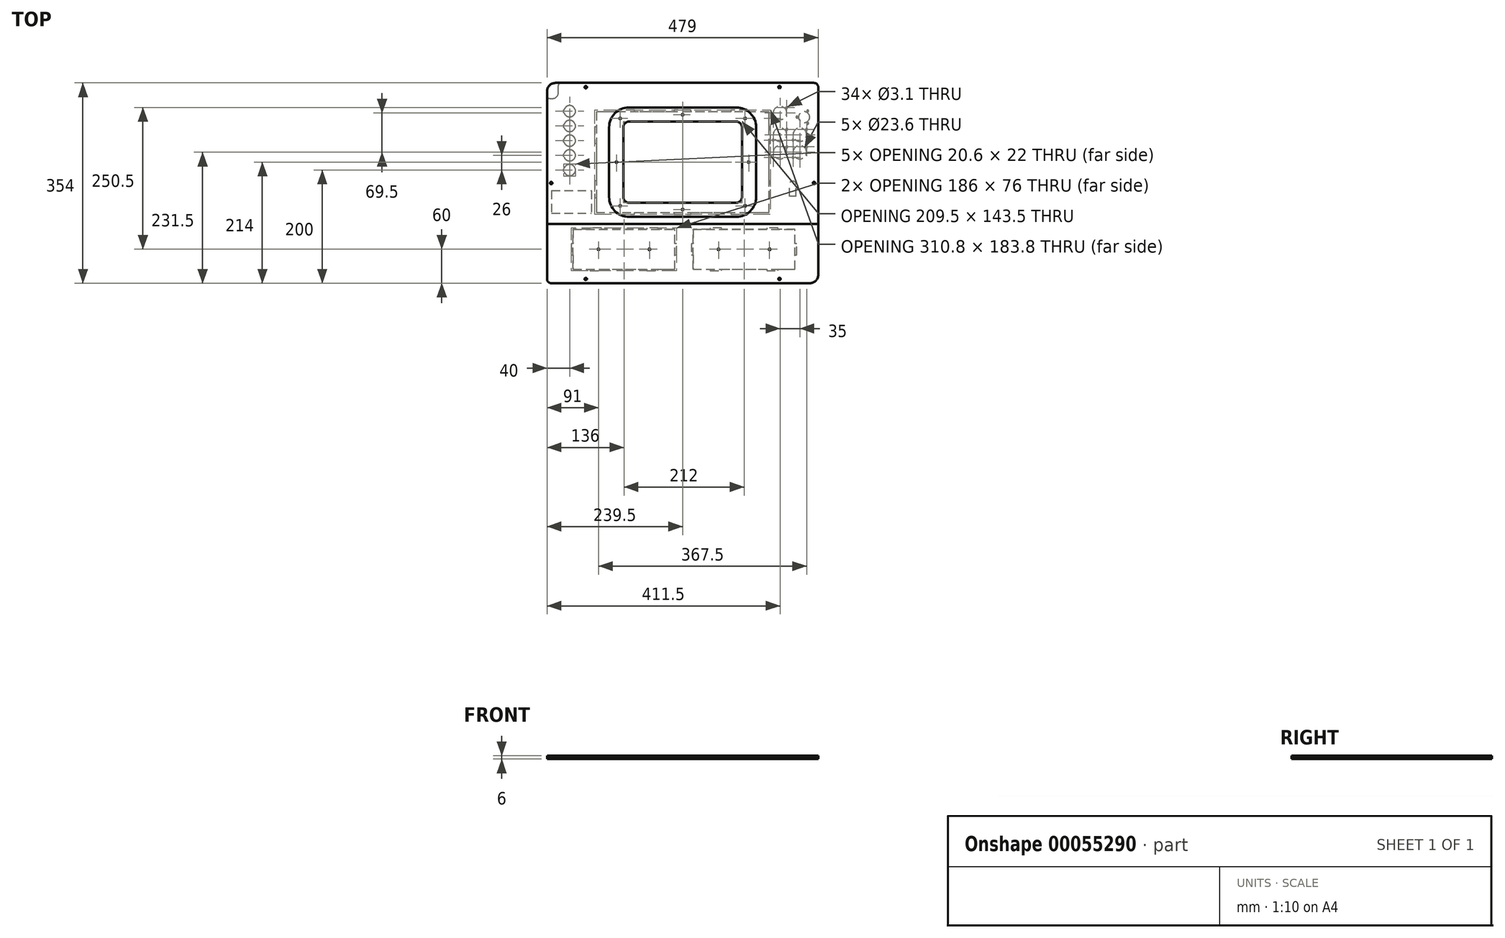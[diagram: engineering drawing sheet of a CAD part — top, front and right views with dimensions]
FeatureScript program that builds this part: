
annotation { "Feature Type Name" : "Feature", "Feature Type Description" : "" }
export const myFeature = defineFeature(function(context is Context, id is Id, definition is map)
    precondition{}
    {
        {
            assignVariable(context, id + "F0", {"name" : "PanelThickness", "anyValue" : 3});
        }
        {
            var Q0;
            Q0=qCreatedBy(makeId("Top.planeOp"),FACE);
            var sketch = newSketch(context, id + "F1", { "sketchPlane" : qUnion([Q0])});
            skPoint(sketch, "E0", {"position": v(168.5, 155) * mm});
            skPoint(sketch, "E1.visualSharp", {"position": v(237, -191.5) * mm});
            skPoint(sketch, "E2.visualSharp", {"position": v(-242, -191.5) * mm});
            skPoint(sketch, "E3.MirrorP", {"position": v(205.63, -175.57) * mm});
            skLineSegment(sketch, "E4.rect.right", {"start": v(237, 155) * mm, "end": v(237, -176.5) * mm});
            skPoint(sketch, "E5", {"position": v(229.5, -14.5) * mm});
            skPoint(sketch, "E6.visualSharp", {"position": v(-222, 135) * mm});
            skPoint(sketch, "E7.visualSharp", {"position": v(237, 162.5) * mm});
            skLineSegment(sketch, "E8", {"start": v(-249.24, -14.5) * mm, "end": v(312.3, -14.5) * mm, "construction": true});
            skPoint(sketch, "E9", {"position": v(-173.5, 155) * mm});
            skPoint(sketch, "E10.visualSharp", {"position": v(-242, 162.5) * mm});
            skLineSegment(sketch, "E11", {"start": v(0, 162.5) * mm, "end": v(0, -191.5) * mm, "construction": true});
            skLineSegment(sketch, "E12.0", {"start": v(-224.5, 155) * mm, "end": v(224.5, 155) * mm, "construction": true});
            skLineSegment(sketch, "E13.0", {"start": v(-242, -184) * mm, "end": v(224.5, -184) * mm, "construction": true});
            skLineSegment(sketch, "E14.0", {"start": v(-234.5, 162.5) * mm, "end": v(-234.5, -191.5) * mm, "construction": true});
            skLineSegment(sketch, "E4.rect.top", {"start": v(-234.5, -191.5) * mm, "end": v(222, -191.5) * mm});
            skLineSegment(sketch, "E4.rect.left", {"start": v(-242, 130) * mm, "end": v(-242, -184) * mm});
            skPoint(sketch, "E15", {"position": v(-234.5, -14.5) * mm});
            skLineSegment(sketch, "E4.rect.bottom", {"start": v(-217, 162.5) * mm, "end": v(229.5, 162.5) * mm});
            skLineSegment(sketch, "E16", {"start": v(168.5, -197.31) * mm, "end": v(168.5, 217.61) * mm, "construction": true});
            skLineSegment(sketch, "E17", {"start": v(-173.5, 192.32) * mm, "end": v(-173.5, -229.31) * mm, "construction": true});
            skLineSegment(sketch, "E18.0", {"start": v(229.5, 162.5) * mm, "end": v(229.5, -191.5) * mm, "construction": true});
            skLineSegment(sketch, "E19.left", {"start": v(-242, 146.2) * mm, "end": v(-242, 155) * mm, "construction": true});
            skLineSegment(sketch, "E19.bottom", {"start": v(-237, 135) * mm, "end": v(-232, 135) * mm});
            skCircle(sketch, "E20", {"center": v(-173.5, -184) * mm, "radius": 2.1 * mm});
            skArc(sketch, "E7.filletArc", {"start": v(237, 155) * mm, "mid": v(234.8, 160.3) * mm, "end": v(229.5, 162.5) * mm});
            skArc(sketch, "E6.filletArc", {"start": v(-232, 135) * mm, "mid": v(-224.93, 137.93) * mm, "end": v(-222, 145) * mm});
            skCircle(sketch, "E21", {"center": v(168.5, 155) * mm, "radius": 2.1 * mm});
            skCircle(sketch, "E22", {"center": v(229.5, -14.5) * mm, "radius": 2.1 * mm});
            skCircle(sketch, "E23", {"center": v(168.5, -184) * mm, "radius": 2.1 * mm});
            skCircle(sketch, "E24", {"center": v(-234.5, -14.5) * mm, "radius": 2.1 * mm});
            skCircle(sketch, "E25", {"center": v(-173.5, 155) * mm, "radius": 2.1 * mm});
            skArc(sketch, "E2.filletArc", {"start": v(-242, -184) * mm, "mid": v(-239.8, -189.3) * mm, "end": v(-234.5, -191.5) * mm});
            skArc(sketch, "E1.filletArc", {"start": v(222, -191.5) * mm, "mid": v(232.6, -187.1) * mm, "end": v(237, -176.5) * mm});
            skLineSegment(sketch, "E19.right", {"start": v(-222, 145) * mm, "end": v(-222, 157.5) * mm});
            skArc(sketch, "E26.filletArc", {"start": v(-237, 135) * mm, "mid": v(-240.54, 133.54) * mm, "end": v(-242, 130) * mm});
            skArc(sketch, "E27.filletArc", {"start": v(-217, 162.5) * mm, "mid": v(-220.54, 161.04) * mm, "end": v(-222, 157.5) * mm});
            skPoint(sketch, "E28", {"position": v(0, -14.5) * mm});
            skLineSegment(sketch, "E29", {"start": v(-242, 140) * mm, "end": v(-242, 130) * mm, "construction": true});
            skLineSegment(sketch, "E30", {"start": v(-234.5, 162.5) * mm, "end": v(-217, 162.5) * mm, "construction": true});
            skLineSegment(sketch, "E31", {"start": v(-242, 130) * mm, "end": v(-242, 147.5) * mm});
            skLineSegment(sketch, "E32", {"start": v(-227, 162.5) * mm, "end": v(-217, 162.5) * mm});
            skArc(sketch, "E33.filletArc", {"start": v(-227, 162.5) * mm, "mid": v(-237.6, 158.1) * mm, "end": v(-242, 147.5) * mm});
            skSolve(sketch);
        }
        {
            var Q0;
            Q0=qCreatedBy(makeId("Top.planeOp"),FACE);
            var sketch = newSketch(context, id + "F2", { "sketchPlane" : qUnion([Q0])});
            skLineSegment(sketch, "E34.bottom", {"start": v(-234, -28) * mm, "end": v(-163.5, -28) * mm});
            skLineSegment(sketch, "E34.top", {"start": v(-234, -67.5) * mm, "end": v(-163.5, -67.5) * mm});
            skLineSegment(sketch, "E34.right", {"start": v(-163.5, -28) * mm, "end": v(-163.5, -67.5) * mm});
            skLineSegment(sketch, "E34.left", {"start": v(-234, -28) * mm, "end": v(-234, -67.5) * mm});
            skLineSegment(sketch, "E35.0", {"start": v(-242, 130) * mm, "end": v(-242, -184) * mm});
            skLineSegment(sketch, "E36.0", {"start": v(-217, 162.5) * mm, "end": v(229.5, 162.5) * mm});
            skLineSegment(sketch, "E37.1", {"start": v(-238.1, -25.9) * mm, "end": v(-159.4, -25.9) * mm, "construction": true});
            skLineSegment(sketch, "E38.0", {"start": v(-159.4, -25.9) * mm, "end": v(-159.4, -69.6) * mm, "construction": true});
            skLineSegment(sketch, "E39.0", {"start": v(-238.1, -25.9) * mm, "end": v(-238.1, -69.6) * mm, "construction": true});
            skLineSegment(sketch, "E40.0", {"start": v(-238.1, -69.6) * mm, "end": v(-159.4, -69.6) * mm, "construction": true});
            skSolve(sketch);
        }
        {
            var Q0;
            Q0=qCreatedBy(makeId("Top.planeOp"),FACE);
            var sketch = newSketch(context, id + "F3", { "sketchPlane" : qUnion([Q0])});
            skLineSegment(sketch, "E41", {"start": v(0, 58.76) * mm, "end": v(0, -203.67) * mm, "construction": true});
            skLineSegment(sketch, "E42", {"start": v(-178.62, -14.5) * mm, "end": v(136.76, -14.5) * mm, "construction": true});
            skLineSegment(sketch, "E43", {"start": v(-16, -141.5) * mm, "end": v(-16, -166.5) * mm});
            skLineSegment(sketch, "E44", {"start": v(-166, -96.5) * mm, "end": v(-196, -96.5) * mm});
            skLineSegment(sketch, "E45.0", {"start": v(-13, -93.5) * mm, "end": v(-13, -169.5) * mm, "construction": true});
            skLineSegment(sketch, "E46", {"start": v(-166, -166.5) * mm, "end": v(-196, -166.5) * mm});
            skLineSegment(sketch, "E47.MirrorCS", {"start": v(-66, -93.5) * mm, "end": v(-46, -93.5) * mm});
            skLineSegment(sketch, "E48.rect.bottom", {"start": v(-16, -96.5) * mm, "end": v(-46, -96.5) * mm});
            skLineSegment(sketch, "E48.rect.top", {"start": v(-16, -166.5) * mm, "end": v(-46, -166.5) * mm});
            skLineSegment(sketch, "E48.rect.left", {"start": v(-16, -96.5) * mm, "end": v(-16, -121.5) * mm});
            skLineSegment(sketch, "E48.rect.right", {"start": v(-196, -96.5) * mm, "end": v(-196, -121.5) * mm});
            skPoint(sketch, "E49", {"position": v(-199, -131.5) * mm});
            skLineSegment(sketch, "E50.top", {"start": v(-66, -169.5) * mm, "end": v(-46, -169.5) * mm});
            skLineSegment(sketch, "E51.MirrorCS", {"start": v(-146, -169.5) * mm, "end": v(-166, -169.5) * mm});
            skLineSegment(sketch, "E52", {"start": v(-66, -96.5) * mm, "end": v(-146, -96.5) * mm});
            skLineSegment(sketch, "E53.0", {"start": v(-13, -169.5) * mm, "end": v(-199, -169.5) * mm, "construction": true});
            skLineSegment(sketch, "E54.0", {"start": v(-199, -93.5) * mm, "end": v(-199, -169.5) * mm, "construction": true});
            skLineSegment(sketch, "E55.0", {"start": v(-13, -93.5) * mm, "end": v(-199, -93.5) * mm, "construction": true});
            skLineSegment(sketch, "E56", {"start": v(-196, -141.5) * mm, "end": v(-196, -166.5) * mm});
            skLineSegment(sketch, "E57.MirrorCS", {"start": v(-13, -141.5) * mm, "end": v(-13, -121.5) * mm});
            skLineSegment(sketch, "E58", {"start": v(-66, -166.5) * mm, "end": v(-146, -166.5) * mm});
            skLineSegment(sketch, "E59.right", {"start": v(-199, -141.5) * mm, "end": v(-199, -121.5) * mm});
            skLineSegment(sketch, "E60.MirrorCS", {"start": v(-16, -121.5) * mm, "end": v(-13, -121.5) * mm});
            skLineSegment(sketch, "E61.MirrorCS", {"start": v(-16, -141.5) * mm, "end": v(-13, -141.5) * mm});
            skLineSegment(sketch, "E59.top", {"start": v(-196, -121.5) * mm, "end": v(-199, -121.5) * mm});
            skLineSegment(sketch, "E62.MirrorCS", {"start": v(-66, -96.5) * mm, "end": v(-66, -93.5) * mm});
            skLineSegment(sketch, "E63.MirrorCS", {"start": v(-46, -96.5) * mm, "end": v(-46, -93.5) * mm});
            skLineSegment(sketch, "E50.left", {"start": v(-66, -166.5) * mm, "end": v(-66, -169.5) * mm});
            skLineSegment(sketch, "E50.right", {"start": v(-46, -166.5) * mm, "end": v(-46, -169.5) * mm});
            skLineSegment(sketch, "E64.MirrorCS", {"start": v(-146, -166.5) * mm, "end": v(-146, -169.5) * mm});
            skLineSegment(sketch, "E65.MirrorCS", {"start": v(-166, -166.5) * mm, "end": v(-166, -169.5) * mm});
            skLineSegment(sketch, "E59.bottom", {"start": v(-196, -141.5) * mm, "end": v(-199, -141.5) * mm});
            skLineSegment(sketch, "E66.MirrorCS", {"start": v(16, -121.5) * mm, "end": v(13, -121.5) * mm});
            skLineSegment(sketch, "E67.MirrorCS", {"start": v(16, -141.5) * mm, "end": v(13, -141.5) * mm});
            skPoint(sketch, "E68.MirrorP", {"position": v(199, -131.5) * mm});
            skLineSegment(sketch, "E69.MirrorCS", {"start": v(146, -96.5) * mm, "end": v(146, -93.5) * mm});
            skLineSegment(sketch, "E70.MirrorCS", {"start": v(199, -93.5) * mm, "end": v(199, -169.5) * mm, "construction": true});
            skLineSegment(sketch, "E71.MirrorCS", {"start": v(166, -96.5) * mm, "end": v(166, -93.5) * mm});
            skLineSegment(sketch, "E72.MirrorCS", {"start": v(13, -93.5) * mm, "end": v(199, -93.5) * mm, "construction": true});
            skLineSegment(sketch, "E73.MirrorCS", {"start": v(196, -141.5) * mm, "end": v(199, -141.5) * mm});
            skLineSegment(sketch, "E74.MirrorCS", {"start": v(16, -141.5) * mm, "end": v(16, -166.5) * mm});
            skLineSegment(sketch, "E75.MirrorCS", {"start": v(196, -141.5) * mm, "end": v(196, -166.5) * mm});
            skLineSegment(sketch, "E76.MirrorCS", {"start": v(13, -141.5) * mm, "end": v(13, -121.5) * mm});
            skLineSegment(sketch, "E77.MirrorCS", {"start": v(166, -96.5) * mm, "end": v(196, -96.5) * mm});
            skLineSegment(sketch, "E78.MirrorCS", {"start": v(66, -166.5) * mm, "end": v(146, -166.5) * mm});
            skLineSegment(sketch, "E79.MirrorCS", {"start": v(13, -93.5) * mm, "end": v(13, -169.5) * mm, "construction": true});
            skLineSegment(sketch, "E80.MirrorCS", {"start": v(199, -141.5) * mm, "end": v(199, -121.5) * mm});
            skLineSegment(sketch, "E81.MirrorCS", {"start": v(166, -166.5) * mm, "end": v(196, -166.5) * mm});
            skLineSegment(sketch, "E82.MirrorCS", {"start": v(13, -169.5) * mm, "end": v(199, -169.5) * mm, "construction": true});
            skLineSegment(sketch, "E83.MirrorCS", {"start": v(66, -93.5) * mm, "end": v(46, -93.5) * mm});
            skLineSegment(sketch, "E84.MirrorCS", {"start": v(16, -96.5) * mm, "end": v(46, -96.5) * mm});
            skLineSegment(sketch, "E85.MirrorCS", {"start": v(66, -96.5) * mm, "end": v(66, -93.5) * mm});
            skLineSegment(sketch, "E86.MirrorCS", {"start": v(16, -96.5) * mm, "end": v(16, -121.5) * mm});
            skLineSegment(sketch, "E87.MirrorCS", {"start": v(46, -96.5) * mm, "end": v(46, -93.5) * mm});
            skLineSegment(sketch, "E88.MirrorCS", {"start": v(196, -96.5) * mm, "end": v(196, -121.5) * mm});
            skLineSegment(sketch, "E89.MirrorCS", {"start": v(66, -166.5) * mm, "end": v(66, -169.5) * mm});
            skLineSegment(sketch, "E90.MirrorCS", {"start": v(66, -169.5) * mm, "end": v(46, -169.5) * mm});
            skLineSegment(sketch, "E91.MirrorCS", {"start": v(46, -166.5) * mm, "end": v(46, -169.5) * mm});
            skLineSegment(sketch, "E92.MirrorCS", {"start": v(146, -169.5) * mm, "end": v(166, -169.5) * mm});
            skLineSegment(sketch, "E93.MirrorCS", {"start": v(146, -166.5) * mm, "end": v(146, -169.5) * mm});
            skLineSegment(sketch, "E94.MirrorCS", {"start": v(146, -93.5) * mm, "end": v(166, -93.5) * mm});
            skLineSegment(sketch, "E95.MirrorCS", {"start": v(16, -166.5) * mm, "end": v(46, -166.5) * mm});
            skLineSegment(sketch, "E96.MirrorCS", {"start": v(196, -121.5) * mm, "end": v(199, -121.5) * mm});
            skLineSegment(sketch, "E97.MirrorCS", {"start": v(66, -96.5) * mm, "end": v(146, -96.5) * mm});
            skLineSegment(sketch, "E98.MirrorCS", {"start": v(166, -166.5) * mm, "end": v(166, -169.5) * mm});
            skPoint(sketch, "E99", {"position": v(0, -14.5) * mm});
            skLineSegment(sketch, "E100", {"start": v(-199, -131.5) * mm, "end": v(-13, -131.5) * mm, "construction": true});
            skLineSegment(sketch, "E101.MirrorCS", {"start": v(-166, -96.5) * mm, "end": v(-166, -93.5) * mm});
            skLineSegment(sketch, "E102.MirrorCS", {"start": v(-146, -93.5) * mm, "end": v(-166, -93.5) * mm});
            skLineSegment(sketch, "E103.MirrorCS", {"start": v(-146, -96.5) * mm, "end": v(-146, -93.5) * mm});
            skPoint(sketch, "E104", {"position": v(-106, -131.5) * mm});
            skLineSegment(sketch, "E105", {"start": v(-106, -96.5) * mm, "end": v(-106, -166.5) * mm, "construction": true});
            skLineSegment(sketch, "E106.0", {"start": v(-249.24, -14.5) * mm, "end": v(312.3, -14.5) * mm, "construction": true});
            skSolve(sketch);
        }
        {
            var Q0;
            Q0=qCreatedBy(makeId("Top.planeOp"),FACE);
            var sketch = newSketch(context, id + "F4", { "sketchPlane" : qUnion([Q0])});
            skLineSegment(sketch, "E107.0", {"start": v(-242, 130) * mm, "end": v(-242, -184) * mm});
            skLineSegment(sketch, "E107.1", {"start": v(-217, 162.5) * mm, "end": v(229.5, 162.5) * mm});
            skPoint(sketch, "E108", {"position": v(-202, 115.3) * mm});
            skPoint(sketch, "E109", {"position": v(-200.95, 112.5) * mm});
            skPoint(sketch, "E110", {"position": v(-202, 109.7) * mm});
            skArc(sketch, "E111", {"start": v(-200.95, 102.56) * mm, "mid": v(-195.59, 104.83) * mm, "end": v(-192.4, 109.7) * mm});
            skArc(sketch, "E112", {"start": v(-211.6, 109.7) * mm, "mid": v(-208.41, 104.83) * mm, "end": v(-203.05, 102.56) * mm});
            skArc(sketch, "E113", {"start": v(-192.4, 115.3) * mm, "mid": v(-195.59, 120.17) * mm, "end": v(-200.95, 122.44) * mm});
            skPoint(sketch, "E114", {"position": v(-203.05, 112.5) * mm});
            skArc(sketch, "E115", {"start": v(-203.05, 122.44) * mm, "mid": v(-208.41, 120.17) * mm, "end": v(-211.6, 115.3) * mm});
            skCircle(sketch, "E116", {"center": v(-202, 112.5) * mm, "radius": 11.5 * mm, "construction": true});
            skLineSegment(sketch, "E117", {"start": v(-192.4, 115.3) * mm, "end": v(-211.6, 115.3) * mm, "construction": true});
            skLineSegment(sketch, "E118", {"start": v(-200.95, 122.44) * mm, "end": v(-200.95, 102.56) * mm, "construction": true});
            skLineSegment(sketch, "E119", {"start": v(-192.4, 109.7) * mm, "end": v(-211.6, 109.7) * mm, "construction": true});
            skLineSegment(sketch, "E120", {"start": v(-203.05, 122.44) * mm, "end": v(-203.05, 102.56) * mm, "construction": true});
            skLineSegment(sketch, "E121", {"start": v(-191.7, 112.5) * mm, "end": v(-212.3, 112.5) * mm, "construction": true});
            skLineSegment(sketch, "E122", {"start": v(-202, 123.5) * mm, "end": v(-202, 101.5) * mm, "construction": true});
            skLineSegment(sketch, "E123", {"start": v(-192.4, 115.3) * mm, "end": v(-191.7, 115.3) * mm});
            skLineSegment(sketch, "E124", {"start": v(-211.6, 115.3) * mm, "end": v(-212.3, 115.3) * mm});
            skLineSegment(sketch, "E125", {"start": v(-203.05, 102.56) * mm, "end": v(-203.05, 101.5) * mm});
            skLineSegment(sketch, "E126", {"start": v(-200.95, 101.5) * mm, "end": v(-203.05, 101.5) * mm});
            skLineSegment(sketch, "E127.rect.right", {"start": v(-212.3, 109.7) * mm, "end": v(-212.3, 115.3) * mm});
            skLineSegment(sketch, "E127.rect.left", {"start": v(-191.7, 109.7) * mm, "end": v(-191.7, 115.3) * mm});
            skLineSegment(sketch, "E127.rect.bottom", {"start": v(-191.7, 109.7) * mm, "end": v(-192.4, 109.7) * mm});
            skLineSegment(sketch, "E128", {"start": v(-211.6, 109.7) * mm, "end": v(-212.3, 109.7) * mm});
            skLineSegment(sketch, "E129", {"start": v(-200.95, 102.56) * mm, "end": v(-200.95, 101.5) * mm});
            skLineSegment(sketch, "E130.MirrorCS", {"start": v(-203.05, 122.44) * mm, "end": v(-203.05, 123.5) * mm});
            skLineSegment(sketch, "E131.MirrorCS", {"start": v(-200.95, 122.44) * mm, "end": v(-200.95, 123.5) * mm});
            skLineSegment(sketch, "E132.MirrorCS", {"start": v(-200.95, 123.5) * mm, "end": v(-203.05, 123.5) * mm});
            skCircle(sketch, "E133.0.1.0", {"center": v(-202, 86.5) * mm, "radius": 11.5 * mm, "construction": true});
            skPoint(sketch, "E133.0.1.1", {"position": v(-203.05, 86.5) * mm});
            skLineSegment(sketch, "E133.0.1.2", {"start": v(-202, 97.5) * mm, "end": v(-202, 75.5) * mm, "construction": true});
            skArc(sketch, "E133.0.1.3", {"start": v(-200.95, 76.56) * mm, "mid": v(-195.59, 78.83) * mm, "end": v(-192.4, 83.7) * mm});
            skLineSegment(sketch, "E133.0.1.4", {"start": v(-212.3, 83.7) * mm, "end": v(-212.3, 89.3) * mm});
            skLineSegment(sketch, "E133.0.1.5", {"start": v(-200.95, 96.44) * mm, "end": v(-200.95, 76.56) * mm, "construction": true});
            skArc(sketch, "E133.0.1.6", {"start": v(-203.05, 96.44) * mm, "mid": v(-208.41, 94.17) * mm, "end": v(-211.6, 89.3) * mm});
            skLineSegment(sketch, "E133.0.1.7", {"start": v(-191.7, 86.5) * mm, "end": v(-212.3, 86.5) * mm, "construction": true});
            skLineSegment(sketch, "E133.0.1.8", {"start": v(-203.05, 96.44) * mm, "end": v(-203.05, 76.56) * mm, "construction": true});
            skPoint(sketch, "E133.0.1.9", {"position": v(-202, 83.7) * mm});
            skPoint(sketch, "E133.0.1.10", {"position": v(-202, 86.5) * mm});
            skArc(sketch, "E133.0.1.11", {"start": v(-192.4, 89.3) * mm, "mid": v(-195.59, 94.17) * mm, "end": v(-200.95, 96.44) * mm});
            skPoint(sketch, "E133.0.1.12", {"position": v(-200.95, 86.5) * mm});
            skLineSegment(sketch, "E133.0.1.13", {"start": v(-192.4, 89.3) * mm, "end": v(-211.6, 89.3) * mm, "construction": true});
            skPoint(sketch, "E133.0.1.14", {"position": v(-202, 89.3) * mm});
            skLineSegment(sketch, "E133.0.1.15", {"start": v(-191.7, 83.7) * mm, "end": v(-191.7, 89.3) * mm});
            skLineSegment(sketch, "E133.0.1.16", {"start": v(-192.4, 83.7) * mm, "end": v(-211.6, 83.7) * mm, "construction": true});
            skArc(sketch, "E133.0.1.17", {"start": v(-211.6, 83.7) * mm, "mid": v(-208.41, 78.83) * mm, "end": v(-203.05, 76.56) * mm});
            skPoint(sketch, "E133.0.1.18", {"position": v(-202, 86.5) * mm});
            skLineSegment(sketch, "E133.0.1.19", {"start": v(-200.95, 75.5) * mm, "end": v(-203.05, 75.5) * mm});
            skLineSegment(sketch, "E133.0.1.20", {"start": v(-192.4, 89.3) * mm, "end": v(-191.7, 89.3) * mm});
            skLineSegment(sketch, "E133.0.1.21", {"start": v(-200.95, 97.5) * mm, "end": v(-203.05, 97.5) * mm});
            skLineSegment(sketch, "E133.0.1.22", {"start": v(-203.05, 96.44) * mm, "end": v(-203.05, 97.5) * mm});
            skLineSegment(sketch, "E133.0.1.23", {"start": v(-203.05, 76.56) * mm, "end": v(-203.05, 75.5) * mm});
            skLineSegment(sketch, "E133.0.1.24", {"start": v(-191.7, 83.7) * mm, "end": v(-192.4, 83.7) * mm});
            skLineSegment(sketch, "E133.0.1.25", {"start": v(-200.95, 76.56) * mm, "end": v(-200.95, 75.5) * mm});
            skLineSegment(sketch, "E133.0.1.26", {"start": v(-211.6, 83.7) * mm, "end": v(-212.3, 83.7) * mm});
            skLineSegment(sketch, "E133.0.1.27", {"start": v(-200.95, 96.44) * mm, "end": v(-200.95, 97.5) * mm});
            skLineSegment(sketch, "E133.0.1.28", {"start": v(-211.6, 89.3) * mm, "end": v(-212.3, 89.3) * mm});
            skCircle(sketch, "E133.0.2.0", {"center": v(-202, 60.5) * mm, "radius": 11.5 * mm, "construction": true});
            skPoint(sketch, "E133.0.2.1", {"position": v(-203.05, 60.5) * mm});
            skLineSegment(sketch, "E133.0.2.2", {"start": v(-202, 71.5) * mm, "end": v(-202, 49.5) * mm, "construction": true});
            skArc(sketch, "E133.0.2.3", {"start": v(-200.95, 50.56) * mm, "mid": v(-195.59, 52.83) * mm, "end": v(-192.4, 57.7) * mm});
            skLineSegment(sketch, "E133.0.2.4", {"start": v(-212.3, 57.7) * mm, "end": v(-212.3, 63.3) * mm});
            skLineSegment(sketch, "E133.0.2.5", {"start": v(-200.95, 70.44) * mm, "end": v(-200.95, 50.56) * mm, "construction": true});
            skArc(sketch, "E133.0.2.6", {"start": v(-203.05, 70.44) * mm, "mid": v(-208.41, 68.17) * mm, "end": v(-211.6, 63.3) * mm});
            skLineSegment(sketch, "E133.0.2.7", {"start": v(-191.7, 60.5) * mm, "end": v(-212.3, 60.5) * mm, "construction": true});
            skLineSegment(sketch, "E133.0.2.8", {"start": v(-203.05, 70.44) * mm, "end": v(-203.05, 50.56) * mm, "construction": true});
            skPoint(sketch, "E133.0.2.9", {"position": v(-202, 57.7) * mm});
            skPoint(sketch, "E133.0.2.10", {"position": v(-202, 60.5) * mm});
            skArc(sketch, "E133.0.2.11", {"start": v(-192.4, 63.3) * mm, "mid": v(-195.59, 68.17) * mm, "end": v(-200.95, 70.44) * mm});
            skPoint(sketch, "E133.0.2.12", {"position": v(-200.95, 60.5) * mm});
            skLineSegment(sketch, "E133.0.2.13", {"start": v(-192.4, 63.3) * mm, "end": v(-211.6, 63.3) * mm, "construction": true});
            skPoint(sketch, "E133.0.2.14", {"position": v(-202, 63.3) * mm});
            skLineSegment(sketch, "E133.0.2.15", {"start": v(-191.7, 57.7) * mm, "end": v(-191.7, 63.3) * mm});
            skLineSegment(sketch, "E133.0.2.16", {"start": v(-192.4, 57.7) * mm, "end": v(-211.6, 57.7) * mm, "construction": true});
            skArc(sketch, "E133.0.2.17", {"start": v(-211.6, 57.7) * mm, "mid": v(-208.41, 52.83) * mm, "end": v(-203.05, 50.56) * mm});
            skPoint(sketch, "E133.0.2.18", {"position": v(-202, 60.5) * mm});
            skLineSegment(sketch, "E133.0.2.19", {"start": v(-200.95, 49.5) * mm, "end": v(-203.05, 49.5) * mm});
            skLineSegment(sketch, "E133.0.2.20", {"start": v(-192.4, 63.3) * mm, "end": v(-191.7, 63.3) * mm});
            skLineSegment(sketch, "E133.0.2.21", {"start": v(-200.95, 71.5) * mm, "end": v(-203.05, 71.5) * mm});
            skLineSegment(sketch, "E133.0.2.22", {"start": v(-203.05, 70.44) * mm, "end": v(-203.05, 71.5) * mm});
            skLineSegment(sketch, "E133.0.2.23", {"start": v(-203.05, 50.56) * mm, "end": v(-203.05, 49.5) * mm});
            skLineSegment(sketch, "E133.0.2.24", {"start": v(-191.7, 57.7) * mm, "end": v(-192.4, 57.7) * mm});
            skLineSegment(sketch, "E133.0.2.25", {"start": v(-200.95, 50.56) * mm, "end": v(-200.95, 49.5) * mm});
            skLineSegment(sketch, "E133.0.2.26", {"start": v(-211.6, 57.7) * mm, "end": v(-212.3, 57.7) * mm});
            skLineSegment(sketch, "E133.0.2.27", {"start": v(-200.95, 70.44) * mm, "end": v(-200.95, 71.5) * mm});
            skLineSegment(sketch, "E133.0.2.28", {"start": v(-211.6, 63.3) * mm, "end": v(-212.3, 63.3) * mm});
            skCircle(sketch, "E133.0.3.0", {"center": v(-202, 34.5) * mm, "radius": 11.5 * mm, "construction": true});
            skPoint(sketch, "E133.0.3.1", {"position": v(-203.05, 34.5) * mm});
            skLineSegment(sketch, "E133.0.3.2", {"start": v(-202, 45.5) * mm, "end": v(-202, 23.5) * mm, "construction": true});
            skArc(sketch, "E133.0.3.3", {"start": v(-200.95, 24.56) * mm, "mid": v(-195.59, 26.83) * mm, "end": v(-192.4, 31.7) * mm});
            skLineSegment(sketch, "E133.0.3.4", {"start": v(-212.3, 31.7) * mm, "end": v(-212.3, 37.3) * mm});
            skLineSegment(sketch, "E133.0.3.5", {"start": v(-200.95, 44.44) * mm, "end": v(-200.95, 24.56) * mm, "construction": true});
            skArc(sketch, "E133.0.3.6", {"start": v(-203.05, 44.44) * mm, "mid": v(-208.41, 42.17) * mm, "end": v(-211.6, 37.3) * mm});
            skLineSegment(sketch, "E133.0.3.7", {"start": v(-191.7, 34.5) * mm, "end": v(-212.3, 34.5) * mm, "construction": true});
            skLineSegment(sketch, "E133.0.3.8", {"start": v(-203.05, 44.44) * mm, "end": v(-203.05, 24.56) * mm, "construction": true});
            skPoint(sketch, "E133.0.3.9", {"position": v(-202, 31.7) * mm});
            skPoint(sketch, "E133.0.3.10", {"position": v(-202, 34.5) * mm});
            skArc(sketch, "E133.0.3.11", {"start": v(-192.4, 37.3) * mm, "mid": v(-195.59, 42.17) * mm, "end": v(-200.95, 44.44) * mm});
            skPoint(sketch, "E133.0.3.12", {"position": v(-200.95, 34.5) * mm});
            skLineSegment(sketch, "E133.0.3.13", {"start": v(-192.4, 37.3) * mm, "end": v(-211.6, 37.3) * mm, "construction": true});
            skPoint(sketch, "E133.0.3.14", {"position": v(-202, 37.3) * mm});
            skLineSegment(sketch, "E133.0.3.15", {"start": v(-191.7, 31.7) * mm, "end": v(-191.7, 37.3) * mm});
            skLineSegment(sketch, "E133.0.3.16", {"start": v(-192.4, 31.7) * mm, "end": v(-211.6, 31.7) * mm, "construction": true});
            skArc(sketch, "E133.0.3.17", {"start": v(-211.6, 31.7) * mm, "mid": v(-208.41, 26.83) * mm, "end": v(-203.05, 24.56) * mm});
            skPoint(sketch, "E133.0.3.18", {"position": v(-202, 34.5) * mm});
            skLineSegment(sketch, "E133.0.3.19", {"start": v(-200.95, 23.5) * mm, "end": v(-203.05, 23.5) * mm});
            skLineSegment(sketch, "E133.0.3.20", {"start": v(-192.4, 37.3) * mm, "end": v(-191.7, 37.3) * mm});
            skLineSegment(sketch, "E133.0.3.21", {"start": v(-200.95, 45.5) * mm, "end": v(-203.05, 45.5) * mm});
            skLineSegment(sketch, "E133.0.3.22", {"start": v(-203.05, 44.44) * mm, "end": v(-203.05, 45.5) * mm});
            skLineSegment(sketch, "E133.0.3.23", {"start": v(-203.05, 24.56) * mm, "end": v(-203.05, 23.5) * mm});
            skLineSegment(sketch, "E133.0.3.24", {"start": v(-191.7, 31.7) * mm, "end": v(-192.4, 31.7) * mm});
            skLineSegment(sketch, "E133.0.3.25", {"start": v(-200.95, 24.56) * mm, "end": v(-200.95, 23.5) * mm});
            skLineSegment(sketch, "E133.0.3.26", {"start": v(-211.6, 31.7) * mm, "end": v(-212.3, 31.7) * mm});
            skLineSegment(sketch, "E133.0.3.27", {"start": v(-200.95, 44.44) * mm, "end": v(-200.95, 45.5) * mm});
            skLineSegment(sketch, "E133.0.3.28", {"start": v(-211.6, 37.3) * mm, "end": v(-212.3, 37.3) * mm});
            skLineSegment(sketch, "E133.direction1", {"start": v(-202, 112.5) * mm, "end": v(-181.18, 112.5) * mm, "construction": true});
            skLineSegment(sketch, "E133.direction2", {"start": v(-202, 112.5) * mm, "end": v(-202, 86.5) * mm, "construction": true});
            skCircle(sketch, "E134.0.0.4", {"center": v(-202, 8.5) * mm, "radius": 11.5 * mm, "construction": true});
            skPoint(sketch, "E134.2.0.4", {"position": v(-203.05, 8.5) * mm});
            skLineSegment(sketch, "E134.3.0.4", {"start": v(-202, 19.5) * mm, "end": v(-202, -2.5) * mm, "construction": true});
            skArc(sketch, "E134.6.0.4", {"start": v(-200.95, -1.44) * mm, "mid": v(-195.59, 0.83) * mm, "end": v(-192.4, 5.7) * mm});
            skLineSegment(sketch, "E134.10.0.4", {"start": v(-212.3, 5.7) * mm, "end": v(-212.3, 11.3) * mm});
            skLineSegment(sketch, "E134.13.0.4", {"start": v(-200.95, 18.44) * mm, "end": v(-200.95, -1.44) * mm, "construction": true});
            skArc(sketch, "E134.16.0.4", {"start": v(-203.05, 18.44) * mm, "mid": v(-208.41, 16.17) * mm, "end": v(-211.6, 11.3) * mm});
            skLineSegment(sketch, "E134.20.0.4", {"start": v(-191.7, 8.5) * mm, "end": v(-212.3, 8.5) * mm, "construction": true});
            skLineSegment(sketch, "E134.23.0.4", {"start": v(-203.05, 18.44) * mm, "end": v(-203.05, -1.44) * mm, "construction": true});
            skPoint(sketch, "E134.26.0.4", {"position": v(-202, 5.7) * mm});
            skPoint(sketch, "E134.27.0.4", {"position": v(-202, 8.5) * mm});
            skArc(sketch, "E134.28.0.4", {"start": v(-192.4, 11.3) * mm, "mid": v(-195.59, 16.17) * mm, "end": v(-200.95, 18.44) * mm});
            skPoint(sketch, "E134.32.0.4", {"position": v(-200.95, 8.5) * mm});
            skLineSegment(sketch, "E134.33.0.4", {"start": v(-192.4, 11.3) * mm, "end": v(-211.6, 11.3) * mm, "construction": true});
            skPoint(sketch, "E134.36.0.4", {"position": v(-202, 11.3) * mm});
            skLineSegment(sketch, "E134.37.0.4", {"start": v(-191.7, 5.7) * mm, "end": v(-191.7, 11.3) * mm});
            skLineSegment(sketch, "E134.40.0.4", {"start": v(-192.4, 5.7) * mm, "end": v(-211.6, 5.7) * mm, "construction": true});
            skArc(sketch, "E134.43.0.4", {"start": v(-211.6, 5.7) * mm, "mid": v(-208.41, 0.83) * mm, "end": v(-203.05, -1.44) * mm});
            skPoint(sketch, "E134.47.0.4", {"position": v(-202, 8.5) * mm});
            skLineSegment(sketch, "E134.48.0.4", {"start": v(-200.95, -2.5) * mm, "end": v(-203.05, -2.5) * mm});
            skLineSegment(sketch, "E134.51.0.4", {"start": v(-192.4, 11.3) * mm, "end": v(-191.7, 11.3) * mm});
            skLineSegment(sketch, "E134.54.0.4", {"start": v(-200.95, 19.5) * mm, "end": v(-203.05, 19.5) * mm});
            skLineSegment(sketch, "E134.57.0.4", {"start": v(-203.05, 18.44) * mm, "end": v(-203.05, 19.5) * mm});
            skLineSegment(sketch, "E134.60.0.4", {"start": v(-203.05, -1.44) * mm, "end": v(-203.05, -2.5) * mm});
            skLineSegment(sketch, "E134.63.0.4", {"start": v(-191.7, 5.7) * mm, "end": v(-192.4, 5.7) * mm});
            skLineSegment(sketch, "E134.66.0.4", {"start": v(-200.95, -1.44) * mm, "end": v(-200.95, -2.5) * mm});
            skLineSegment(sketch, "E134.69.0.4", {"start": v(-211.6, 5.7) * mm, "end": v(-212.3, 5.7) * mm});
            skLineSegment(sketch, "E134.72.0.4", {"start": v(-200.95, 18.44) * mm, "end": v(-200.95, 19.5) * mm});
            skLineSegment(sketch, "E134.75.0.4", {"start": v(-211.6, 11.3) * mm, "end": v(-212.3, 11.3) * mm});
            skSolve(sketch);
        }
        {
            var Q0;
            Q0=qCreatedBy(makeId("Top.planeOp"),FACE);
            var sketch = newSketch(context, id + "F5", { "sketchPlane" : qUnion([Q0])});
            skLineSegment(sketch, "E135", {"start": v(204.5, 59.2) * mm, "end": v(204.5, 132.46) * mm, "construction": true});
            skLineSegment(sketch, "E136.left", {"start": v(204.5, 71) * mm, "end": v(204.5, 84) * mm, "construction": true});
            skLineSegment(sketch, "E137.0", {"start": v(237, 155) * mm, "end": v(237, -176.5) * mm});
            skLineSegment(sketch, "E137.1", {"start": v(-217, 162.5) * mm, "end": v(229.5, 162.5) * mm});
            skCircle(sketch, "E138", {"center": v(212, 102) * mm, "radius": 12.5 * mm, "construction": true});
            skCircle(sketch, "E139", {"center": v(212, 102) * mm, "radius": 16 * mm, "construction": true});
            skCircle(sketch, "E140", {"center": v(199.5, 102) * mm, "radius": 1.75 * mm});
            skCircle(sketch, "E141.1.0", {"center": v(218.25, 91.17) * mm, "radius": 1.75 * mm});
            skCircle(sketch, "E141.2.0", {"center": v(218.25, 112.83) * mm, "radius": 1.75 * mm});
            skCircle(sketch, "E142", {"center": v(212, 102) * mm, "radius": 9.75 * mm});
            skPoint(sketch, "E143", {"position": v(177, 109.5) * mm});
            skLineSegment(sketch, "E144.MirrorCS", {"start": v(154, 109.5) * mm, "end": v(154, 96.5) * mm, "construction": true});
            skLineSegment(sketch, "E145.MirrorCS", {"start": v(169.5, 96.5) * mm, "end": v(154, 96.5) * mm, "construction": true});
            skLineSegment(sketch, "E146.MirrorCS", {"start": v(169.5, 96.5) * mm, "end": v(185, 96.5) * mm, "construction": true});
            skLineSegment(sketch, "E147.MirrorCS", {"start": v(185, 109.5) * mm, "end": v(185, 96.5) * mm, "construction": true});
            skLineSegment(sketch, "E148.left", {"start": v(169.5, 109.5) * mm, "end": v(169.5, 122.5) * mm, "construction": true});
            skLineSegment(sketch, "E148.top", {"start": v(169.5, 122.5) * mm, "end": v(154, 122.5) * mm, "construction": true});
            skLineSegment(sketch, "E148.bottom", {"start": v(169.5, 109.5) * mm, "end": v(161.52, 109.5) * mm, "construction": true});
            skLineSegment(sketch, "E149", {"start": v(169.5, 97.7) * mm, "end": v(169.5, 109.5) * mm, "construction": true});
            skCircle(sketch, "E150.MirrorC", {"center": v(169.5, 109.5) * mm, "radius": 11.8 * mm});
            skLineSegment(sketch, "E151", {"start": v(163.94, 109.5) * mm, "end": v(185, 109.5) * mm, "construction": true});
            skLineSegment(sketch, "E152.MirrorCS", {"start": v(185, 109.5) * mm, "end": v(185, 122.5) * mm, "construction": true});
            skLineSegment(sketch, "E148.right", {"start": v(154, 109.5) * mm, "end": v(154, 122.5) * mm, "construction": true});
            skLineSegment(sketch, "E153.MirrorCS", {"start": v(157.5, 95.86) * mm, "end": v(157.5, 88.51) * mm, "construction": true});
            skLineSegment(sketch, "E154.MirrorCS", {"start": v(192.3, 119) * mm, "end": v(186.5, 119) * mm, "construction": true});
            skLineSegment(sketch, "E155.MirrorCS", {"start": v(181.5, 114.86) * mm, "end": v(181.5, 108.38) * mm, "construction": true});
            skLineSegment(sketch, "E156.MirrorCS", {"start": v(169.5, 122.5) * mm, "end": v(185, 122.5) * mm, "construction": true});
            skCircle(sketch, "E157.MirrorC", {"center": v(181.5, 119) * mm, "radius": 1.55 * mm});
            skCircle(sketch, "E158.MirrorC", {"center": v(157.5, 100) * mm, "radius": 1.55 * mm});
            skLineSegment(sketch, "E159.MirrorCS", {"start": v(166.3, 100) * mm, "end": v(162.5, 100) * mm, "construction": true});
            skLineSegment(sketch, "E160.0.1.0", {"start": v(169.5, 66.7) * mm, "end": v(169.5, 78.5) * mm, "construction": true});
            skLineSegment(sketch, "E160.0.1.1", {"start": v(156.44, 71) * mm, "end": v(182.56, 71) * mm, "construction": true});
            skLineSegment(sketch, "E160.0.1.2", {"start": v(169.5, 91.5) * mm, "end": v(154, 91.5) * mm, "construction": true});
            skLineSegment(sketch, "E160.0.1.3", {"start": v(169.5, 78.5) * mm, "end": v(169.5, 91.5) * mm, "construction": true});
            skLineSegment(sketch, "E160.0.1.4", {"start": v(185, 71) * mm, "end": v(185, 58) * mm, "construction": true});
            skLineSegment(sketch, "E160.0.1.5", {"start": v(154, 78.5) * mm, "end": v(154, 91.5) * mm, "construction": true});
            skLineSegment(sketch, "E160.0.1.6", {"start": v(181.5, 83.86) * mm, "end": v(181.5, 77.38) * mm, "construction": true});
            skLineSegment(sketch, "E160.0.1.7", {"start": v(169.5, 84) * mm, "end": v(185, 84) * mm, "construction": true});
            skCircle(sketch, "E160.0.1.8", {"center": v(157.5, 61.5) * mm, "radius": 1.55 * mm});
            skLineSegment(sketch, "E160.0.1.9", {"start": v(184.8, 80.5) * mm, "end": v(179, 80.5) * mm, "construction": true});
            skCircle(sketch, "E160.0.1.10", {"center": v(169.5, 71) * mm, "radius": 11.8 * mm});
            skLineSegment(sketch, "E160.0.1.11", {"start": v(185, 71) * mm, "end": v(185, 84) * mm, "construction": true});
            skLineSegment(sketch, "E160.0.1.12", {"start": v(157.5, 64.86) * mm, "end": v(157.5, 57.51) * mm, "construction": true});
            skCircle(sketch, "E160.0.1.13", {"center": v(181.5, 80.5) * mm, "radius": 1.55 * mm});
            skLineSegment(sketch, "E160.0.1.14", {"start": v(169.5, 78.5) * mm, "end": v(154.02, 78.5) * mm, "construction": true});
            skLineSegment(sketch, "E160.0.1.15", {"start": v(169.5, 58) * mm, "end": v(185, 58) * mm, "construction": true});
            skLineSegment(sketch, "E160.0.1.16", {"start": v(169.5, 58) * mm, "end": v(154, 58) * mm, "construction": true});
            skLineSegment(sketch, "E160.0.1.17", {"start": v(154, 71) * mm, "end": v(154, 58) * mm, "construction": true});
            skPoint(sketch, "E160.0.1.18", {"position": v(169.5, 71) * mm});
            skLineSegment(sketch, "E160.0.1.19", {"start": v(158.8, 61.5) * mm, "end": v(155, 61.5) * mm, "construction": true});
            skCircle(sketch, "E160.0.1.20", {"center": v(169.5, 78.5) * mm, "radius": 11.8 * mm});
            skLineSegment(sketch, "E160.0.2.0", {"start": v(169.5, 28.2) * mm, "end": v(169.5, 40) * mm, "construction": true});
            skLineSegment(sketch, "E160.0.2.1", {"start": v(156.44, 40) * mm, "end": v(182.56, 40) * mm, "construction": true});
            skLineSegment(sketch, "E160.0.2.2", {"start": v(169.5, 53) * mm, "end": v(154, 53) * mm, "construction": true});
            skLineSegment(sketch, "E160.0.2.3", {"start": v(169.5, 40) * mm, "end": v(169.5, 53) * mm, "construction": true});
            skLineSegment(sketch, "E160.0.2.4", {"start": v(185, 40) * mm, "end": v(185, 27) * mm, "construction": true});
            skLineSegment(sketch, "E160.0.2.5", {"start": v(154, 40) * mm, "end": v(154, 53) * mm, "construction": true});
            skLineSegment(sketch, "E160.0.2.6", {"start": v(181.5, 52.86) * mm, "end": v(181.5, 46.38) * mm, "construction": true});
            skLineSegment(sketch, "E160.0.2.7", {"start": v(169.5, 53) * mm, "end": v(185, 53) * mm, "construction": true});
            skCircle(sketch, "E160.0.2.8", {"center": v(157.5, 30.5) * mm, "radius": 1.55 * mm});
            skLineSegment(sketch, "E160.0.2.9", {"start": v(184.8, 49.5) * mm, "end": v(179, 49.5) * mm, "construction": true});
            skCircle(sketch, "E160.0.2.10", {"center": v(169.5, 40) * mm, "radius": 11.8 * mm});
            skLineSegment(sketch, "E160.0.2.11", {"start": v(185, 40) * mm, "end": v(185, 53) * mm, "construction": true});
            skLineSegment(sketch, "E160.0.2.12", {"start": v(157.5, 33.86) * mm, "end": v(157.5, 26.51) * mm, "construction": true});
            skCircle(sketch, "E160.0.2.13", {"center": v(181.5, 49.5) * mm, "radius": 1.55 * mm});
            skLineSegment(sketch, "E160.0.2.14", {"start": v(169.5, 40) * mm, "end": v(154.02, 40) * mm, "construction": true});
            skLineSegment(sketch, "E160.0.2.15", {"start": v(169.5, 27) * mm, "end": v(185, 27) * mm, "construction": true});
            skLineSegment(sketch, "E160.0.2.16", {"start": v(169.5, 27) * mm, "end": v(154, 27) * mm, "construction": true});
            skLineSegment(sketch, "E160.0.2.17", {"start": v(154, 40) * mm, "end": v(154, 27) * mm, "construction": true});
            skPoint(sketch, "E160.0.2.18", {"position": v(169.5, 40) * mm});
            skLineSegment(sketch, "E160.0.2.19", {"start": v(158.8, 30.5) * mm, "end": v(155, 30.5) * mm, "construction": true});
            skCircle(sketch, "E160.0.2.20", {"center": v(169.5, 40) * mm, "radius": 11.8 * mm});
            skLineSegment(sketch, "E160.1.0.0", {"start": v(212, 89.5) * mm, "end": v(212, 102) * mm, "construction": true});
            skLineSegment(sketch, "E160.1.0.1", {"start": v(198.94, 102) * mm, "end": v(225.06, 102) * mm, "construction": true});
            skLineSegment(sketch, "E160.1.0.3", {"start": v(212, 102) * mm, "end": v(212, 114.5) * mm, "construction": true});
            skLineSegment(sketch, "E160.1.1.0", {"start": v(204.5, 59.2) * mm, "end": v(204.5, 71) * mm, "construction": true});
            skLineSegment(sketch, "E160.1.1.1", {"start": v(191.44, 71) * mm, "end": v(217.56, 71) * mm, "construction": true});
            skLineSegment(sketch, "E160.1.1.2", {"start": v(204.5, 84) * mm, "end": v(189, 84) * mm, "construction": true});
            skLineSegment(sketch, "E160.1.1.4", {"start": v(220, 71) * mm, "end": v(220, 58) * mm, "construction": true});
            skLineSegment(sketch, "E160.1.1.5", {"start": v(189, 71) * mm, "end": v(189, 84) * mm, "construction": true});
            skLineSegment(sketch, "E160.1.1.6", {"start": v(216.5, 83.86) * mm, "end": v(216.5, 77.38) * mm, "construction": true});
            skLineSegment(sketch, "E160.1.1.7", {"start": v(204.5, 84) * mm, "end": v(220, 84) * mm, "construction": true});
            skCircle(sketch, "E160.1.1.8", {"center": v(192.5, 61.5) * mm, "radius": 1.55 * mm});
            skLineSegment(sketch, "E160.1.1.9", {"start": v(219.8, 80.5) * mm, "end": v(214, 80.5) * mm, "construction": true});
            skCircle(sketch, "E160.1.1.10", {"center": v(204.5, 71) * mm, "radius": 11.8 * mm});
            skLineSegment(sketch, "E160.1.1.11", {"start": v(220, 71) * mm, "end": v(220, 84) * mm, "construction": true});
            skLineSegment(sketch, "E160.1.1.12", {"start": v(192.5, 64.86) * mm, "end": v(192.5, 57.51) * mm, "construction": true});
            skCircle(sketch, "E160.1.1.13", {"center": v(216.5, 80.5) * mm, "radius": 1.55 * mm});
            skLineSegment(sketch, "E160.1.1.14", {"start": v(204.5, 71) * mm, "end": v(189.02, 71) * mm, "construction": true});
            skLineSegment(sketch, "E160.1.1.15", {"start": v(204.5, 58) * mm, "end": v(220, 58) * mm, "construction": true});
            skLineSegment(sketch, "E160.1.1.16", {"start": v(204.5, 58) * mm, "end": v(189, 58) * mm, "construction": true});
            skLineSegment(sketch, "E160.1.1.17", {"start": v(189, 71) * mm, "end": v(189, 58) * mm, "construction": true});
            skPoint(sketch, "E160.1.1.18", {"position": v(204.5, 71) * mm});
            skLineSegment(sketch, "E160.1.1.19", {"start": v(193.8, 61.5) * mm, "end": v(190, 61.5) * mm, "construction": true});
            skCircle(sketch, "E160.1.1.20", {"center": v(204.5, 71) * mm, "radius": 11.8 * mm});
            skLineSegment(sketch, "E160.1.2.0", {"start": v(204.5, 28.2) * mm, "end": v(204.5, 40) * mm, "construction": true});
            skLineSegment(sketch, "E160.1.2.1", {"start": v(191.44, 40) * mm, "end": v(217.56, 40) * mm, "construction": true});
            skLineSegment(sketch, "E160.1.2.2", {"start": v(204.5, 53) * mm, "end": v(189, 53) * mm, "construction": true});
            skLineSegment(sketch, "E160.1.2.3", {"start": v(204.5, 40) * mm, "end": v(204.5, 53) * mm, "construction": true});
            skLineSegment(sketch, "E160.1.2.4", {"start": v(220, 40) * mm, "end": v(220, 27) * mm, "construction": true});
            skLineSegment(sketch, "E160.1.2.5", {"start": v(189, 40) * mm, "end": v(189, 53) * mm, "construction": true});
            skLineSegment(sketch, "E160.1.2.6", {"start": v(216.5, 52.86) * mm, "end": v(216.5, 46.38) * mm, "construction": true});
            skLineSegment(sketch, "E160.1.2.7", {"start": v(204.5, 53) * mm, "end": v(220, 53) * mm, "construction": true});
            skCircle(sketch, "E160.1.2.8", {"center": v(192.5, 30.5) * mm, "radius": 1.55 * mm});
            skLineSegment(sketch, "E160.1.2.9", {"start": v(219.8, 49.5) * mm, "end": v(214, 49.5) * mm, "construction": true});
            skCircle(sketch, "E160.1.2.10", {"center": v(204.5, 40) * mm, "radius": 11.8 * mm});
            skLineSegment(sketch, "E160.1.2.11", {"start": v(220, 40) * mm, "end": v(220, 53) * mm, "construction": true});
            skLineSegment(sketch, "E160.1.2.12", {"start": v(192.5, 33.86) * mm, "end": v(192.5, 26.51) * mm, "construction": true});
            skCircle(sketch, "E160.1.2.13", {"center": v(216.5, 49.5) * mm, "radius": 1.55 * mm});
            skLineSegment(sketch, "E160.1.2.14", {"start": v(204.5, 40) * mm, "end": v(189.02, 40) * mm, "construction": true});
            skLineSegment(sketch, "E160.1.2.15", {"start": v(204.5, 27) * mm, "end": v(220, 27) * mm, "construction": true});
            skLineSegment(sketch, "E160.1.2.16", {"start": v(204.5, 27) * mm, "end": v(189, 27) * mm, "construction": true});
            skLineSegment(sketch, "E160.1.2.17", {"start": v(189, 40) * mm, "end": v(189, 27) * mm, "construction": true});
            skPoint(sketch, "E160.1.2.18", {"position": v(204.5, 40) * mm});
            skLineSegment(sketch, "E160.1.2.19", {"start": v(193.8, 30.5) * mm, "end": v(190, 30.5) * mm, "construction": true});
            skCircle(sketch, "E160.1.2.20", {"center": v(204.5, 40) * mm, "radius": 11.8 * mm});
            skLineSegment(sketch, "E160.direction2", {"start": v(169.5, 97.7) * mm, "end": v(169.5, 66.7) * mm, "construction": true});
            skSolve(sketch);
        }
        {
            var Q0;
            Q0=qCreatedBy(makeId("Top.planeOp"),FACE);
            var sketch = newSketch(context, id + "F6", { "sketchPlane" : qUnion([Q0])});
            skLineSegment(sketch, "E161.rect.bottom", {"start": v(149.9, 111.4) * mm, "end": v(112.5, 111.4) * mm});
            skLineSegment(sketch, "E161.rect.top", {"start": v(149.9, -66.4) * mm, "end": v(112.5, -66.4) * mm});
            skLineSegment(sketch, "E161.rect.left", {"start": v(149.9, 111.4) * mm, "end": v(149.9, 85.5) * mm});
            skLineSegment(sketch, "E161.rect.right", {"start": v(-154.9, 111.4) * mm, "end": v(-154.9, 85.5) * mm});
            skLineSegment(sketch, "E162.0", {"start": v(152.9, -69.4) * mm, "end": v(-157.9, -69.4) * mm, "construction": true});
            skLineSegment(sketch, "E163.0", {"start": v(152.9, 114.4) * mm, "end": v(152.9, -69.4) * mm, "construction": true});
            skLineSegment(sketch, "E164.0", {"start": v(-157.9, 114.4) * mm, "end": v(-157.9, -69.4) * mm, "construction": true});
            skLineSegment(sketch, "E165.0", {"start": v(152.9, 114.4) * mm, "end": v(-157.9, 114.4) * mm, "construction": true});
            skLineSegment(sketch, "E166.bottom", {"start": v(-17.5, -69.4) * mm, "end": v(-2.5, -69.4) * mm});
            skLineSegment(sketch, "E166.top", {"start": v(-17.5, -66.4) * mm, "end": v(-2.5, -66.4) * mm, "construction": true});
            skLineSegment(sketch, "E166.left", {"start": v(-17.5, -69.4) * mm, "end": v(-17.5, -66.4) * mm});
            skLineSegment(sketch, "E166.right", {"start": v(-2.5, -69.4) * mm, "end": v(-2.5, -66.4) * mm, "construction": true});
            skLineSegment(sketch, "E167.bottom", {"start": v(-117.5, -69.4) * mm, "end": v(-87.5, -69.4) * mm});
            skLineSegment(sketch, "E167.left", {"start": v(-117.5, -69.4) * mm, "end": v(-117.5, -66.4) * mm});
            skLineSegment(sketch, "E167.right", {"start": v(-87.5, -69.4) * mm, "end": v(-87.5, -66.4) * mm});
            skPoint(sketch, "E168", {"position": v(-102.5, -69.4) * mm});
            skLineSegment(sketch, "E169.bottom", {"start": v(-157.9, -40.5) * mm, "end": v(-154.9, -40.5) * mm});
            skLineSegment(sketch, "E169.top", {"start": v(-157.9, -10.5) * mm, "end": v(-154.9, -10.5) * mm});
            skLineSegment(sketch, "E169.left", {"start": v(-157.9, -40.5) * mm, "end": v(-157.9, -10.5) * mm});
            skPoint(sketch, "E170", {"position": v(-157.9, -25.5) * mm});
            skLineSegment(sketch, "E171.MirrorCS", {"start": v(152.9, -40.5) * mm, "end": v(149.9, -40.5) * mm});
            skLineSegment(sketch, "E172.MirrorCS", {"start": v(152.9, -40.5) * mm, "end": v(152.9, -10.5) * mm});
            skLineSegment(sketch, "E173.MirrorCS", {"start": v(152.9, -10.5) * mm, "end": v(149.9, -10.5) * mm});
            skLineSegment(sketch, "E174.MirrorCS", {"start": v(112.5, -69.4) * mm, "end": v(82.5, -69.4) * mm});
            skLineSegment(sketch, "E175.MirrorCS", {"start": v(82.5, -69.4) * mm, "end": v(82.5, -66.4) * mm});
            skLineSegment(sketch, "E176.MirrorCS", {"start": v(112.5, -69.4) * mm, "end": v(112.5, -66.4) * mm});
            skLineSegment(sketch, "E177.MirrorCS", {"start": v(12.5, -69.4) * mm, "end": v(12.5, -66.4) * mm});
            skLineSegment(sketch, "E178.MirrorCS", {"start": v(12.5, -69.4) * mm, "end": v(-2.5, -69.4) * mm});
            skLineSegment(sketch, "E179", {"start": v(-154.9, -10.5) * mm, "end": v(-154.9, -40.5) * mm, "construction": true});
            skLineSegment(sketch, "E180", {"start": v(-154.9, -40.5) * mm, "end": v(-154.9, -66.4) * mm});
            skLineSegment(sketch, "E181", {"start": v(-117.5, -66.4) * mm, "end": v(-154.9, -66.4) * mm});
            skLineSegment(sketch, "E182", {"start": v(-17.5, -66.4) * mm, "end": v(-87.5, -66.4) * mm});
            skLineSegment(sketch, "E183", {"start": v(82.5, -66.4) * mm, "end": v(12.5, -66.4) * mm});
            skLineSegment(sketch, "E184", {"start": v(149.9, -40.5) * mm, "end": v(149.9, -66.4) * mm});
            skLineSegment(sketch, "E185.MirrorCS", {"start": v(-157.9, 85.5) * mm, "end": v(-157.9, 55.5) * mm});
            skLineSegment(sketch, "E186.MirrorCS", {"start": v(-17.5, 114.4) * mm, "end": v(-17.5, 111.4) * mm});
            skLineSegment(sketch, "E187.MirrorCS", {"start": v(-17.5, 114.4) * mm, "end": v(-2.5, 114.4) * mm});
            skLineSegment(sketch, "E188.MirrorCS", {"start": v(12.5, 114.4) * mm, "end": v(12.5, 111.4) * mm});
            skLineSegment(sketch, "E189.MirrorCS", {"start": v(12.5, 114.4) * mm, "end": v(-2.5, 114.4) * mm});
            skLineSegment(sketch, "E190.MirrorCS", {"start": v(-117.5, 114.4) * mm, "end": v(-87.5, 114.4) * mm});
            skLineSegment(sketch, "E191.MirrorCS", {"start": v(-87.5, 114.4) * mm, "end": v(-87.5, 111.4) * mm});
            skLineSegment(sketch, "E192.MirrorCS", {"start": v(-117.5, 114.4) * mm, "end": v(-117.5, 111.4) * mm});
            skLineSegment(sketch, "E193.MirrorCS", {"start": v(82.5, 114.4) * mm, "end": v(82.5, 111.4) * mm});
            skLineSegment(sketch, "E194.MirrorCS", {"start": v(112.5, 114.4) * mm, "end": v(82.5, 114.4) * mm});
            skLineSegment(sketch, "E195.MirrorCS", {"start": v(112.5, 114.4) * mm, "end": v(112.5, 111.4) * mm});
            skLineSegment(sketch, "E196.MirrorCS", {"start": v(152.9, 85.5) * mm, "end": v(149.9, 85.5) * mm});
            skLineSegment(sketch, "E197.MirrorCS", {"start": v(152.9, 85.5) * mm, "end": v(152.9, 55.5) * mm});
            skLineSegment(sketch, "E198.MirrorCS", {"start": v(152.9, 55.5) * mm, "end": v(149.9, 55.5) * mm});
            skLineSegment(sketch, "E199", {"start": v(149.9, 55.5) * mm, "end": v(149.9, -10.5) * mm});
            skLineSegment(sketch, "E200", {"start": v(149.9, 85.5) * mm, "end": v(149.9, 55.5) * mm, "construction": true});
            skLineSegment(sketch, "E201", {"start": v(112.5, 111.4) * mm, "end": v(82.5, 111.4) * mm, "construction": true});
            skLineSegment(sketch, "E202", {"start": v(82.5, 111.4) * mm, "end": v(12.5, 111.4) * mm});
            skLineSegment(sketch, "E203", {"start": v(12.5, 111.4) * mm, "end": v(-17.5, 111.4) * mm, "construction": true});
            skLineSegment(sketch, "E204", {"start": v(-17.5, 111.4) * mm, "end": v(-87.5, 111.4) * mm});
            skLineSegment(sketch, "E205", {"start": v(-87.5, 111.4) * mm, "end": v(-117.5, 111.4) * mm, "construction": true});
            skLineSegment(sketch, "E206", {"start": v(-117.5, 111.4) * mm, "end": v(-154.9, 111.4) * mm});
            skLineSegment(sketch, "E207", {"start": v(-154.9, 85.5) * mm, "end": v(-154.9, 55.5) * mm, "construction": true});
            skLineSegment(sketch, "E208", {"start": v(-154.9, 55.5) * mm, "end": v(-154.9, -10.5) * mm});
            skLineSegment(sketch, "E209", {"start": v(149.9, 85.5) * mm, "end": v(149.9, 55.5) * mm});
            skLineSegment(sketch, "E210", {"start": v(-17.5, 111.4) * mm, "end": v(12.5, 111.4) * mm});
            skLineSegment(sketch, "E211", {"start": v(-87.5, 111.4) * mm, "end": v(-117.5, 111.4) * mm});
            skLineSegment(sketch, "E212", {"start": v(-154.9, 85.5) * mm, "end": v(-154.9, 55.5) * mm});
            skLineSegment(sketch, "E213", {"start": v(-154.9, -40.5) * mm, "end": v(-154.9, -10.5) * mm});
            skLineSegment(sketch, "E214", {"start": v(-117.5, -66.4) * mm, "end": v(-87.5, -66.4) * mm});
            skLineSegment(sketch, "E215", {"start": v(-17.5, -66.4) * mm, "end": v(12.5, -66.4) * mm});
            skLineSegment(sketch, "E216", {"start": v(82.5, -66.4) * mm, "end": v(112.5, -66.4) * mm});
            skLineSegment(sketch, "E217", {"start": v(149.9, -40.5) * mm, "end": v(149.9, -10.5) * mm});
            skLineSegment(sketch, "E218", {"start": v(82.5, 111.4) * mm, "end": v(112.5, 111.4) * mm});
            skLineSegment(sketch, "E219", {"start": v(-157.9, 22.5) * mm, "end": v(152.9, 22.5) * mm, "construction": true});
            skLineSegment(sketch, "E220", {"start": v(-2.5, 114.4) * mm, "end": v(-2.5, -69.4) * mm, "construction": true});
            skPoint(sketch, "E221", {"position": v(-2.5, 22.5) * mm});
            skLineSegment(sketch, "E222", {"start": v(-157.9, 55.5) * mm, "end": v(-154.9, 55.5) * mm});
            skLineSegment(sketch, "E223", {"start": v(-157.9, 85.5) * mm, "end": v(-154.9, 85.5) * mm});
            skPoint(sketch, "E224", {"position": v(-2.5, -66.4) * mm});
            skLineSegment(sketch, "E225.0", {"start": v(-242, 130) * mm, "end": v(-242, -184) * mm});
            skLineSegment(sketch, "E225.1", {"start": v(-217, 162.5) * mm, "end": v(229.5, 162.5) * mm});
            skSolve(sketch);
        }
        {
            var Q0;
            Q0=qCreatedBy(makeId("Top.planeOp"),FACE);
            var sketch = newSketch(context, id + "F7", { "sketchPlane" : qUnion([Q0])});
            skLineSegment(sketch, "E226", {"start": v(-2.5, 206.06) * mm, "end": v(-2.5, -186.6) * mm, "construction": true});
            skLineSegment(sketch, "E227.bottom", {"start": v(-97.25, -49.25) * mm, "end": v(92.25, -49.25) * mm});
            skLineSegment(sketch, "E227.top", {"start": v(-97.25, 94.25) * mm, "end": v(92.25, 94.25) * mm});
            skLineSegment(sketch, "E227.left", {"start": v(-107.25, -39.25) * mm, "end": v(-107.25, 84.25) * mm});
            skLineSegment(sketch, "E227.right", {"start": v(102.25, -39.25) * mm, "end": v(102.25, 84.25) * mm});
            skPoint(sketch, "E228", {"position": v(-2.5, -49.25) * mm});
            skLineSegment(sketch, "E229", {"start": v(-132.25, 22.5) * mm, "end": v(127.25, 22.5) * mm, "construction": true});
            skPoint(sketch, "E230", {"position": v(-2.5, 22.5) * mm});
            skPoint(sketch, "E231.visualSharp", {"position": v(-107.25, 94.25) * mm});
            skArc(sketch, "E231.filletArc", {"start": v(-97.25, 94.25) * mm, "mid": v(-104.32, 91.32) * mm, "end": v(-107.25, 84.25) * mm});
            skPoint(sketch, "E232.visualSharp", {"position": v(-107.25, -49.25) * mm});
            skArc(sketch, "E232.filletArc", {"start": v(-107.25, -39.25) * mm, "mid": v(-104.32, -46.32) * mm, "end": v(-97.25, -49.25) * mm});
            skPoint(sketch, "E233.visualSharp", {"position": v(102.25, -49.25) * mm});
            skArc(sketch, "E233.filletArc", {"start": v(92.25, -49.25) * mm, "mid": v(99.32, -46.32) * mm, "end": v(102.25, -39.25) * mm});
            skPoint(sketch, "E234.visualSharp", {"position": v(102.25, 94.25) * mm});
            skArc(sketch, "E234.filletArc", {"start": v(102.25, 84.25) * mm, "mid": v(99.32, 91.32) * mm, "end": v(92.25, 94.25) * mm});
            skCircle(sketch, "E235", {"center": v(-2.5, 106.25) * mm, "radius": 1.55 * mm});
            skCircle(sketch, "E236", {"center": v(107.8, -54.8) * mm, "radius": 1.55 * mm});
            skCircle(sketch, "E237", {"center": v(-2.5, -61.25) * mm, "radius": 1.55 * mm});
            skArc(sketch, "E238.0", {"start": v(-132.25, -39.25) * mm, "mid": v(-122, -64) * mm, "end": v(-97.25, -74.25) * mm});
            skLineSegment(sketch, "E238.1", {"start": v(-132.25, -39.25) * mm, "end": v(-132.25, 84.25) * mm});
            skArc(sketch, "E238.2", {"start": v(-97.25, 119.25) * mm, "mid": v(-122, 109) * mm, "end": v(-132.25, 84.25) * mm});
            skLineSegment(sketch, "E238.3", {"start": v(-97.25, 119.25) * mm, "end": v(92.25, 119.25) * mm});
            skArc(sketch, "E238.4", {"start": v(127.25, 84.25) * mm, "mid": v(117, 109) * mm, "end": v(92.25, 119.25) * mm});
            skLineSegment(sketch, "E238.5", {"start": v(-97.25, -74.25) * mm, "end": v(92.25, -74.25) * mm});
            skLineSegment(sketch, "E238.6", {"start": v(127.25, -39.25) * mm, "end": v(127.25, 84.25) * mm});
            skArc(sketch, "E238.7", {"start": v(92.25, -74.25) * mm, "mid": v(117, -64) * mm, "end": v(127.25, -39.25) * mm});
            skPoint(sketch, "E239", {"position": v(-119.25, 22.5) * mm});
            skPoint(sketch, "E240.orphan", {"position": v(-107.25, 22.5) * mm});
            skPoint(sketch, "E241.orphan", {"position": v(102.25, 22.5) * mm});
            skCircle(sketch, "E242", {"center": v(114.25, 22.5) * mm, "radius": 1.55 * mm});
            skCircle(sketch, "E243", {"center": v(-119.25, 22.5) * mm, "radius": 1.55 * mm});
            skLineSegment(sketch, "E244", {"start": v(127.25, -39.25) * mm, "end": v(127.25, -74.25) * mm, "construction": true});
            skLineSegment(sketch, "E245", {"start": v(92.25, -74.25) * mm, "end": v(127.25, -74.25) * mm, "construction": true});
            skLineSegment(sketch, "E246", {"start": v(92.25, -39.25) * mm, "end": v(127.25, -74.25) * mm, "construction": true});
            skLineSegment(sketch, "E247", {"start": v(-97.25, -61.25) * mm, "end": v(-132.25, -61.25) * mm, "construction": true});
            skLineSegment(sketch, "E248", {"start": v(-119.25, -62.37) * mm, "end": v(-119.25, -74.25) * mm, "construction": true});
            skLineSegment(sketch, "E249", {"start": v(-97.25, -39.25) * mm, "end": v(-132.25, -74.25) * mm, "construction": true});
            skPoint(sketch, "E250", {"position": v(-119.25, -61.25) * mm});
            skPoint(sketch, "E251", {"position": v(-112.8, -54.8) * mm});
            skCircle(sketch, "E252.MirrorC", {"center": v(107.8, 99.8) * mm, "radius": 1.55 * mm});
            skArc(sketch, "E253.0", {"start": v(-119.25, -39.25) * mm, "mid": v(-112.8, -54.8) * mm, "end": v(-97.25, -61.25) * mm, "construction": true});
            skLineSegment(sketch, "E253.1", {"start": v(-119.25, -39.25) * mm, "end": v(-119.25, 84.25) * mm, "construction": true});
            skArc(sketch, "E253.2", {"start": v(-97.25, 106.25) * mm, "mid": v(-112.8, 99.8) * mm, "end": v(-119.25, 84.25) * mm, "construction": true});
            skLineSegment(sketch, "E253.3", {"start": v(-97.25, 106.25) * mm, "end": v(92.25, 106.25) * mm, "construction": true});
            skArc(sketch, "E253.4", {"start": v(114.25, 84.25) * mm, "mid": v(107.8, 99.8) * mm, "end": v(92.25, 106.25) * mm, "construction": true});
            skLineSegment(sketch, "E253.5", {"start": v(-97.25, -61.25) * mm, "end": v(92.25, -61.25) * mm, "construction": true});
            skLineSegment(sketch, "E253.6", {"start": v(114.25, -39.25) * mm, "end": v(114.25, 84.25) * mm, "construction": true});
            skArc(sketch, "E253.7", {"start": v(92.25, -61.25) * mm, "mid": v(107.8, -54.8) * mm, "end": v(114.25, -39.25) * mm, "construction": true});
            skPoint(sketch, "E254", {"position": v(-2.5, 94.25) * mm});
            skCircle(sketch, "E255", {"center": v(-112.8, -54.8) * mm, "radius": 1.55 * mm});
            skCircle(sketch, "E256.MirrorC", {"center": v(-112.8, 99.8) * mm, "radius": 1.55 * mm});
            skLineSegment(sketch, "E257", {"start": v(-97.25, -74.25) * mm, "end": v(-132.25, -74.25) * mm, "construction": true});
            skLineSegment(sketch, "E258", {"start": v(-132.25, -39.25) * mm, "end": v(-132.25, -74.25) * mm, "construction": true});
            skPoint(sketch, "E259", {"position": v(-132.25, -74.25) * mm});
            skLineSegment(sketch, "E260", {"start": v(114.25, -39.25) * mm, "end": v(114.25, -74.25) * mm, "construction": true});
            skLineSegment(sketch, "E261", {"start": v(92.25, -61.25) * mm, "end": v(127.25, -61.25) * mm, "construction": true});
            skLineSegment(sketch, "E262.0", {"start": v(-242, 130) * mm, "end": v(-242, -184) * mm});
            skLineSegment(sketch, "E262.1", {"start": v(-217, 162.5) * mm, "end": v(229.5, 162.5) * mm});
            skSolve(sketch);
        }
        {
            var Q0;
            Q0=qCreatedBy(makeId("Top.planeOp"),FACE);
            var sketch = newSketch(context, id + "F8", { "sketchPlane" : qUnion([Q0])});
            skLineSegment(sketch, "E263.0", {"start": v(-217, 162.5) * mm, "end": v(229.5, 162.5) * mm});
            skLineSegment(sketch, "E263.1", {"start": v(237, 155) * mm, "end": v(237, -176.5) * mm});
            skLineSegment(sketch, "E264.top", {"start": v(157, -87.5) * mm, "end": v(233, -87.5) * mm, "construction": true});
            skLineSegment(sketch, "E264.left", {"start": v(157, -22.5) * mm, "end": v(157, -87.5) * mm, "construction": true});
            skLineSegment(sketch, "E264.right", {"start": v(233, -7.5) * mm, "end": v(233, -87.5) * mm, "construction": true});
            skLineSegment(sketch, "E265.bottom", {"start": v(157, -87.5) * mm, "end": v(227.58, -87.5) * mm, "construction": true});
            skPoint(sketch, "E266.startSnap0", {"position": v(157, -30.86) * mm});
            skLineSegment(sketch, "E267.rect.bottom", {"start": v(198, -38) * mm, "end": v(186, -38) * mm});
            skLineSegment(sketch, "E267.rect.top", {"start": v(198, -17) * mm, "end": v(186, -17) * mm});
            skLineSegment(sketch, "E267.rect.left", {"start": v(198, -38) * mm, "end": v(198, -17) * mm});
            skLineSegment(sketch, "E267.rect.right", {"start": v(186, -38) * mm, "end": v(186, -17) * mm});
            skPoint(sketch, "E267.rect.middle", {"position": v(192, -27.5) * mm});
            skPoint(sketch, "E268", {"position": v(152.67, -30.86) * mm});
            skLineSegment(sketch, "E269", {"start": v(166.58, -22.5) * mm, "end": v(166.58, -87.5) * mm, "construction": true});
            skLineSegment(sketch, "E270", {"start": v(192, -17) * mm, "end": v(192, -87.5) * mm, "construction": true});
            skCircle(sketch, "E271", {"center": v(192, -17) * mm, "radius": 6 * mm});
            skSolve(sketch);
        }
        {
            var Q0;
            Q0=qCreatedBy(makeId("Top.planeOp"),FACE);
            var sketch = newSketch(context, id + "F9", { "sketchPlane" : qUnion([Q0])});
            skLineSegment(sketch, "E272.0", {"start": v(-217, 162.5) * mm, "end": v(229.5, 162.5) * mm});
            skArc(sketch, "E272.1", {"start": v(237, 155) * mm, "mid": v(234.8, 160.3) * mm, "end": v(229.5, 162.5) * mm});
            skLineSegment(sketch, "E272.2", {"start": v(237, 155) * mm, "end": v(237, -176.5) * mm});
            skArc(sketch, "E272.3", {"start": v(222, -191.5) * mm, "mid": v(232.6, -187.1) * mm, "end": v(237, -176.5) * mm});
            skLineSegment(sketch, "E272.4", {"start": v(-234.5, -191.5) * mm, "end": v(222, -191.5) * mm});
            skArc(sketch, "E272.5", {"start": v(-242, -184) * mm, "mid": v(-239.8, -189.3) * mm, "end": v(-234.5, -191.5) * mm});
            skLineSegment(sketch, "E272.6", {"start": v(-242, 130) * mm, "end": v(-242, -184) * mm});
            skArc(sketch, "E272.7", {"start": v(-237, 135) * mm, "mid": v(-240.54, 133.54) * mm, "end": v(-242, 130) * mm});
            skLineSegment(sketch, "E272.8", {"start": v(-237, 135) * mm, "end": v(-232, 135) * mm});
            skArc(sketch, "E272.9", {"start": v(-232, 135) * mm, "mid": v(-224.93, 137.93) * mm, "end": v(-222, 145) * mm});
            skLineSegment(sketch, "E272.10", {"start": v(-222, 145) * mm, "end": v(-222, 157.5) * mm});
            skArc(sketch, "E272.11", {"start": v(-217, 162.5) * mm, "mid": v(-220.54, 161.04) * mm, "end": v(-222, 157.5) * mm});
            skCircle(sketch, "E272.13", {"center": v(-234.5, -14.5) * mm, "radius": 2.1 * mm});
            skCircle(sketch, "E272.14", {"center": v(168.5, 155) * mm, "radius": 2.1 * mm});
            skCircle(sketch, "E272.15", {"center": v(229.5, -14.5) * mm, "radius": 2.1 * mm});
            skCircle(sketch, "E272.16", {"center": v(168.5, -184) * mm, "radius": 2.1 * mm});
            skCircle(sketch, "E272.17", {"center": v(-173.5, -184) * mm, "radius": 2.1 * mm});
            skCircle(sketch, "E272.18", {"center": v(-173.5, 155) * mm, "radius": 2.1 * mm});
            skLineSegment(sketch, "E273.0.0", {"start": v(-16, -166.5) * mm, "end": v(-16, -141.5) * mm});
            skLineSegment(sketch, "E273.0.1", {"start": v(-16, -141.5) * mm, "end": v(-13, -141.5) * mm});
            skLineSegment(sketch, "E273.0.2", {"start": v(-13, -141.5) * mm, "end": v(-13, -121.5) * mm});
            skLineSegment(sketch, "E273.0.3", {"start": v(-13, -121.5) * mm, "end": v(-16, -121.5) * mm});
            skLineSegment(sketch, "E273.0.4", {"start": v(-16, -121.5) * mm, "end": v(-16, -96.5) * mm});
            skLineSegment(sketch, "E273.0.5", {"start": v(-16, -96.5) * mm, "end": v(-46, -96.5) * mm});
            skLineSegment(sketch, "E273.0.6", {"start": v(-46, -96.5) * mm, "end": v(-46, -93.5) * mm});
            skLineSegment(sketch, "E273.0.7", {"start": v(-46, -93.5) * mm, "end": v(-66, -93.5) * mm});
            skLineSegment(sketch, "E273.0.8", {"start": v(-66, -93.5) * mm, "end": v(-66, -96.5) * mm});
            skLineSegment(sketch, "E273.0.9", {"start": v(-66, -96.5) * mm, "end": v(-146, -96.5) * mm});
            skLineSegment(sketch, "E273.0.10", {"start": v(-146, -96.5) * mm, "end": v(-146, -93.5) * mm});
            skLineSegment(sketch, "E273.0.11", {"start": v(-146, -93.5) * mm, "end": v(-166, -93.5) * mm});
            skLineSegment(sketch, "E273.0.12", {"start": v(-166, -93.5) * mm, "end": v(-166, -96.5) * mm});
            skLineSegment(sketch, "E273.0.13", {"start": v(-166, -96.5) * mm, "end": v(-196, -96.5) * mm});
            skLineSegment(sketch, "E273.0.14", {"start": v(-196, -96.5) * mm, "end": v(-196, -121.5) * mm});
            skLineSegment(sketch, "E273.0.15", {"start": v(-196, -121.5) * mm, "end": v(-199, -121.5) * mm});
            skLineSegment(sketch, "E273.0.16", {"start": v(-199, -121.5) * mm, "end": v(-199, -141.5) * mm});
            skLineSegment(sketch, "E273.0.17", {"start": v(-199, -141.5) * mm, "end": v(-196, -141.5) * mm});
            skLineSegment(sketch, "E273.0.18", {"start": v(-196, -141.5) * mm, "end": v(-196, -166.5) * mm});
            skLineSegment(sketch, "E273.0.19", {"start": v(-196, -166.5) * mm, "end": v(-166, -166.5) * mm});
            skLineSegment(sketch, "E273.0.20", {"start": v(-166, -166.5) * mm, "end": v(-166, -169.5) * mm});
            skLineSegment(sketch, "E273.0.21", {"start": v(-166, -169.5) * mm, "end": v(-146, -169.5) * mm});
            skLineSegment(sketch, "E273.0.22", {"start": v(-146, -169.5) * mm, "end": v(-146, -166.5) * mm});
            skLineSegment(sketch, "E273.0.23", {"start": v(-146, -166.5) * mm, "end": v(-66, -166.5) * mm});
            skLineSegment(sketch, "E273.0.24", {"start": v(-66, -166.5) * mm, "end": v(-66, -169.5) * mm});
            skLineSegment(sketch, "E273.0.25", {"start": v(-66, -169.5) * mm, "end": v(-46, -169.5) * mm});
            skLineSegment(sketch, "E273.0.26", {"start": v(-46, -169.5) * mm, "end": v(-46, -166.5) * mm});
            skLineSegment(sketch, "E273.0.27", {"start": v(-46, -166.5) * mm, "end": v(-16, -166.5) * mm});
            skLineSegment(sketch, "E274.1.0", {"start": v(16, -96.5) * mm, "end": v(16, -121.5) * mm});
            skLineSegment(sketch, "E274.1.1", {"start": v(16, -121.5) * mm, "end": v(13, -121.5) * mm});
            skLineSegment(sketch, "E274.1.2", {"start": v(13, -121.5) * mm, "end": v(13, -141.5) * mm});
            skLineSegment(sketch, "E274.1.3", {"start": v(13, -141.5) * mm, "end": v(16, -141.5) * mm});
            skLineSegment(sketch, "E274.1.4", {"start": v(16, -141.5) * mm, "end": v(16, -166.5) * mm});
            skLineSegment(sketch, "E274.1.5", {"start": v(16, -166.5) * mm, "end": v(46, -166.5) * mm});
            skLineSegment(sketch, "E274.1.6", {"start": v(46, -166.5) * mm, "end": v(46, -169.5) * mm});
            skLineSegment(sketch, "E274.1.7", {"start": v(46, -169.5) * mm, "end": v(66, -169.5) * mm});
            skLineSegment(sketch, "E274.1.8", {"start": v(66, -169.5) * mm, "end": v(66, -166.5) * mm});
            skLineSegment(sketch, "E274.1.9", {"start": v(66, -166.5) * mm, "end": v(146, -166.5) * mm});
            skLineSegment(sketch, "E274.1.10", {"start": v(146, -166.5) * mm, "end": v(146, -169.5) * mm});
            skLineSegment(sketch, "E274.1.11", {"start": v(146, -169.5) * mm, "end": v(166, -169.5) * mm});
            skLineSegment(sketch, "E274.1.12", {"start": v(166, -169.5) * mm, "end": v(166, -166.5) * mm});
            skLineSegment(sketch, "E274.1.13", {"start": v(166, -166.5) * mm, "end": v(196, -166.5) * mm});
            skLineSegment(sketch, "E274.1.14", {"start": v(196, -166.5) * mm, "end": v(196, -141.5) * mm});
            skLineSegment(sketch, "E274.1.15", {"start": v(196, -141.5) * mm, "end": v(199, -141.5) * mm});
            skLineSegment(sketch, "E274.1.16", {"start": v(199, -141.5) * mm, "end": v(199, -121.5) * mm});
            skLineSegment(sketch, "E274.1.17", {"start": v(199, -121.5) * mm, "end": v(196, -121.5) * mm});
            skLineSegment(sketch, "E274.1.18", {"start": v(196, -121.5) * mm, "end": v(196, -96.5) * mm});
            skLineSegment(sketch, "E274.1.19", {"start": v(196, -96.5) * mm, "end": v(166, -96.5) * mm});
            skLineSegment(sketch, "E274.1.20", {"start": v(166, -96.5) * mm, "end": v(166, -93.5) * mm});
            skLineSegment(sketch, "E274.1.21", {"start": v(166, -93.5) * mm, "end": v(146, -93.5) * mm});
            skLineSegment(sketch, "E274.1.22", {"start": v(146, -93.5) * mm, "end": v(146, -96.5) * mm});
            skLineSegment(sketch, "E274.1.23", {"start": v(146, -96.5) * mm, "end": v(66, -96.5) * mm});
            skLineSegment(sketch, "E274.1.24", {"start": v(66, -96.5) * mm, "end": v(66, -93.5) * mm});
            skLineSegment(sketch, "E274.1.25", {"start": v(66, -93.5) * mm, "end": v(46, -93.5) * mm});
            skLineSegment(sketch, "E274.1.26", {"start": v(46, -93.5) * mm, "end": v(46, -96.5) * mm});
            skLineSegment(sketch, "E274.1.27", {"start": v(46, -96.5) * mm, "end": v(16, -96.5) * mm});
            skArc(sketch, "E275.0", {"start": v(-211.6, 109.7) * mm, "mid": v(-208.41, 104.83) * mm, "end": v(-203.05, 102.56) * mm});
            skLineSegment(sketch, "E275.1", {"start": v(-212.3, 109.7) * mm, "end": v(-212.3, 115.3) * mm});
            skArc(sketch, "E275.2", {"start": v(-203.05, 122.44) * mm, "mid": v(-208.41, 120.17) * mm, "end": v(-211.6, 115.3) * mm});
            skArc(sketch, "E275.3", {"start": v(-192.4, 115.3) * mm, "mid": v(-195.59, 120.17) * mm, "end": v(-200.95, 122.44) * mm});
            skArc(sketch, "E275.4", {"start": v(-200.95, 102.56) * mm, "mid": v(-195.59, 104.83) * mm, "end": v(-192.4, 109.7) * mm});
            skLineSegment(sketch, "E276.0", {"start": v(-211.6, 115.3) * mm, "end": v(-212.3, 115.3) * mm});
            skLineSegment(sketch, "E276.1", {"start": v(-211.6, 109.7) * mm, "end": v(-212.3, 109.7) * mm});
            skLineSegment(sketch, "E277.2", {"start": v(-192.4, 115.3) * mm, "end": v(-191.7, 115.3) * mm});
            skLineSegment(sketch, "E277.3", {"start": v(-191.7, 109.7) * mm, "end": v(-192.4, 109.7) * mm});
            skLineSegment(sketch, "E277.4", {"start": v(-191.7, 109.7) * mm, "end": v(-191.7, 115.3) * mm});
            skLineSegment(sketch, "E278.0", {"start": v(-203.05, 122.44) * mm, "end": v(-203.05, 123.5) * mm});
            skLineSegment(sketch, "E278.1", {"start": v(-200.95, 123.5) * mm, "end": v(-203.05, 123.5) * mm});
            skLineSegment(sketch, "E278.2", {"start": v(-200.95, 122.44) * mm, "end": v(-200.95, 123.5) * mm});
            skArc(sketch, "E279.0", {"start": v(-203.05, 96.44) * mm, "mid": v(-208.41, 94.17) * mm, "end": v(-211.6, 89.3) * mm});
            skArc(sketch, "E279.1", {"start": v(-192.4, 89.3) * mm, "mid": v(-195.59, 94.17) * mm, "end": v(-200.95, 96.44) * mm});
            skArc(sketch, "E279.2", {"start": v(-200.95, 76.56) * mm, "mid": v(-195.59, 78.83) * mm, "end": v(-192.4, 83.7) * mm});
            skArc(sketch, "E279.3", {"start": v(-211.6, 83.7) * mm, "mid": v(-208.41, 78.83) * mm, "end": v(-203.05, 76.56) * mm});
            skLineSegment(sketch, "E279.4", {"start": v(-212.3, 83.7) * mm, "end": v(-212.3, 89.3) * mm});
            skLineSegment(sketch, "E279.5", {"start": v(-191.7, 83.7) * mm, "end": v(-191.7, 89.3) * mm});
            skLineSegment(sketch, "E279.6", {"start": v(-200.95, 97.5) * mm, "end": v(-203.05, 97.5) * mm});
            skLineSegment(sketch, "E279.7", {"start": v(-200.95, 75.5) * mm, "end": v(-203.05, 75.5) * mm});
            skLineSegment(sketch, "E279.8", {"start": v(-200.95, 76.56) * mm, "end": v(-200.95, 75.5) * mm});
            skLineSegment(sketch, "E279.9", {"start": v(-203.05, 76.56) * mm, "end": v(-203.05, 75.5) * mm});
            skLineSegment(sketch, "E279.10", {"start": v(-203.05, 96.44) * mm, "end": v(-203.05, 97.5) * mm});
            skLineSegment(sketch, "E279.11", {"start": v(-200.95, 96.44) * mm, "end": v(-200.95, 97.5) * mm});
            skLineSegment(sketch, "E279.12", {"start": v(-211.6, 89.3) * mm, "end": v(-212.3, 89.3) * mm});
            skLineSegment(sketch, "E279.13", {"start": v(-192.4, 89.3) * mm, "end": v(-191.7, 89.3) * mm});
            skLineSegment(sketch, "E279.14", {"start": v(-191.7, 83.7) * mm, "end": v(-192.4, 83.7) * mm});
            skLineSegment(sketch, "E279.15", {"start": v(-211.6, 83.7) * mm, "end": v(-212.3, 83.7) * mm});
            skArc(sketch, "E280.0", {"start": v(-200.95, 50.56) * mm, "mid": v(-195.59, 52.83) * mm, "end": v(-192.4, 57.7) * mm});
            skArc(sketch, "E280.1", {"start": v(-203.05, 70.44) * mm, "mid": v(-208.41, 68.17) * mm, "end": v(-211.6, 63.3) * mm});
            skArc(sketch, "E280.2", {"start": v(-211.6, 57.7) * mm, "mid": v(-208.41, 52.83) * mm, "end": v(-203.05, 50.56) * mm});
            skArc(sketch, "E280.3", {"start": v(-192.4, 63.3) * mm, "mid": v(-195.59, 68.17) * mm, "end": v(-200.95, 70.44) * mm});
            skArc(sketch, "E280.4", {"start": v(-203.05, 44.44) * mm, "mid": v(-208.41, 42.17) * mm, "end": v(-211.6, 37.3) * mm});
            skArc(sketch, "E280.5", {"start": v(-192.4, 37.3) * mm, "mid": v(-195.59, 42.17) * mm, "end": v(-200.95, 44.44) * mm});
            skArc(sketch, "E280.6", {"start": v(-200.95, 24.56) * mm, "mid": v(-195.59, 26.83) * mm, "end": v(-192.4, 31.7) * mm});
            skArc(sketch, "E280.7", {"start": v(-211.6, 31.7) * mm, "mid": v(-208.41, 26.83) * mm, "end": v(-203.05, 24.56) * mm});
            skLineSegment(sketch, "E281.0", {"start": v(-212.3, 57.7) * mm, "end": v(-212.3, 63.3) * mm});
            skLineSegment(sketch, "E281.1", {"start": v(-191.7, 57.7) * mm, "end": v(-191.7, 63.3) * mm});
            skLineSegment(sketch, "E281.2", {"start": v(-212.3, 31.7) * mm, "end": v(-212.3, 37.3) * mm});
            skLineSegment(sketch, "E281.3", {"start": v(-191.7, 31.7) * mm, "end": v(-191.7, 37.3) * mm});
            skLineSegment(sketch, "E282.0", {"start": v(-203.05, 70.44) * mm, "end": v(-203.05, 71.5) * mm});
            skLineSegment(sketch, "E282.1", {"start": v(-200.95, 71.5) * mm, "end": v(-203.05, 71.5) * mm});
            skLineSegment(sketch, "E282.2", {"start": v(-200.95, 70.44) * mm, "end": v(-200.95, 71.5) * mm});
            skLineSegment(sketch, "E282.3", {"start": v(-211.6, 57.7) * mm, "end": v(-212.3, 57.7) * mm});
            skLineSegment(sketch, "E282.4", {"start": v(-211.6, 63.3) * mm, "end": v(-212.3, 63.3) * mm});
            skLineSegment(sketch, "E282.5", {"start": v(-192.4, 63.3) * mm, "end": v(-191.7, 63.3) * mm});
            skLineSegment(sketch, "E282.6", {"start": v(-191.7, 57.7) * mm, "end": v(-192.4, 57.7) * mm});
            skLineSegment(sketch, "E283.0", {"start": v(-203.05, 50.56) * mm, "end": v(-203.05, 49.5) * mm});
            skLineSegment(sketch, "E283.1", {"start": v(-200.95, 49.5) * mm, "end": v(-203.05, 49.5) * mm});
            skLineSegment(sketch, "E283.2", {"start": v(-200.95, 50.56) * mm, "end": v(-200.95, 49.5) * mm});
            skLineSegment(sketch, "E283.3", {"start": v(-203.05, 44.44) * mm, "end": v(-203.05, 45.5) * mm});
            skLineSegment(sketch, "E283.4", {"start": v(-200.95, 45.5) * mm, "end": v(-203.05, 45.5) * mm});
            skLineSegment(sketch, "E283.5", {"start": v(-200.95, 44.44) * mm, "end": v(-200.95, 45.5) * mm});
            skLineSegment(sketch, "E284.0", {"start": v(-211.6, 37.3) * mm, "end": v(-212.3, 37.3) * mm});
            skLineSegment(sketch, "E284.1", {"start": v(-211.6, 31.7) * mm, "end": v(-212.3, 31.7) * mm});
            skLineSegment(sketch, "E284.2", {"start": v(-191.7, 31.7) * mm, "end": v(-192.4, 31.7) * mm});
            skLineSegment(sketch, "E284.3", {"start": v(-192.4, 37.3) * mm, "end": v(-191.7, 37.3) * mm});
            skLineSegment(sketch, "E285.0", {"start": v(-203.05, 24.56) * mm, "end": v(-203.05, 23.5) * mm});
            skLineSegment(sketch, "E285.1", {"start": v(-200.95, 23.5) * mm, "end": v(-203.05, 23.5) * mm});
            skLineSegment(sketch, "E285.2", {"start": v(-200.95, 24.56) * mm, "end": v(-200.95, 23.5) * mm});
            skLineSegment(sketch, "E286.0.0", {"start": v(149.9, 85.5) * mm, "end": v(149.9, 111.4) * mm});
            skLineSegment(sketch, "E286.0.1", {"start": v(149.9, 111.4) * mm, "end": v(112.5, 111.4) * mm});
            skLineSegment(sketch, "E286.0.2", {"start": v(112.5, 111.4) * mm, "end": v(82.5, 111.4) * mm});
            skLineSegment(sketch, "E286.0.3", {"start": v(82.5, 111.4) * mm, "end": v(12.5, 111.4) * mm});
            skLineSegment(sketch, "E286.0.4", {"start": v(12.5, 111.4) * mm, "end": v(-17.5, 111.4) * mm});
            skLineSegment(sketch, "E286.0.5", {"start": v(-17.5, 111.4) * mm, "end": v(-87.5, 111.4) * mm});
            skLineSegment(sketch, "E286.0.6", {"start": v(-87.5, 111.4) * mm, "end": v(-117.5, 111.4) * mm});
            skLineSegment(sketch, "E286.0.7", {"start": v(-117.5, 111.4) * mm, "end": v(-154.9, 111.4) * mm});
            skLineSegment(sketch, "E286.0.8", {"start": v(-154.9, 111.4) * mm, "end": v(-154.9, 85.5) * mm});
            skLineSegment(sketch, "E286.0.13", {"start": v(-154.9, -10.5) * mm, "end": v(-154.9, -40.5) * mm});
            skLineSegment(sketch, "E286.0.14", {"start": v(-154.9, -40.5) * mm, "end": v(-154.9, -66.4) * mm});
            skLineSegment(sketch, "E286.0.15", {"start": v(-154.9, -66.4) * mm, "end": v(-117.5, -66.4) * mm});
            skLineSegment(sketch, "E286.0.16", {"start": v(-117.5, -66.4) * mm, "end": v(-87.5, -66.4) * mm});
            skLineSegment(sketch, "E286.0.17", {"start": v(-87.5, -66.4) * mm, "end": v(-17.5, -66.4) * mm});
            skLineSegment(sketch, "E286.0.18", {"start": v(-17.5, -66.4) * mm, "end": v(12.5, -66.4) * mm});
            skLineSegment(sketch, "E286.0.19", {"start": v(12.5, -66.4) * mm, "end": v(82.5, -66.4) * mm});
            skLineSegment(sketch, "E286.0.20", {"start": v(82.5, -66.4) * mm, "end": v(112.5, -66.4) * mm});
            skLineSegment(sketch, "E286.0.21", {"start": v(112.5, -66.4) * mm, "end": v(149.9, -66.4) * mm});
            skLineSegment(sketch, "E286.0.22", {"start": v(149.9, -66.4) * mm, "end": v(149.9, -40.5) * mm});
            skLineSegment(sketch, "E286.0.23", {"start": v(149.9, -40.5) * mm, "end": v(149.9, -10.5) * mm});
            skLineSegment(sketch, "E286.0.24", {"start": v(149.9, -10.5) * mm, "end": v(149.9, 55.5) * mm});
            skLineSegment(sketch, "E286.0.25", {"start": v(149.9, 55.5) * mm, "end": v(149.9, 85.5) * mm});
            skLineSegment(sketch, "E286.1.0", {"start": v(-157.9, -10.5) * mm, "end": v(-157.9, -40.5) * mm});
            skLineSegment(sketch, "E286.1.1", {"start": v(-157.9, -40.5) * mm, "end": v(-154.9, -40.5) * mm});
            skLineSegment(sketch, "E286.1.2", {"start": v(-154.9, -40.5) * mm, "end": v(-154.9, -10.5) * mm});
            skLineSegment(sketch, "E286.1.3", {"start": v(-154.9, -10.5) * mm, "end": v(-157.9, -10.5) * mm});
            skLineSegment(sketch, "E286.2.0", {"start": v(-117.5, -66.4) * mm, "end": v(-117.5, -69.4) * mm});
            skLineSegment(sketch, "E286.2.1", {"start": v(-117.5, -69.4) * mm, "end": v(-87.5, -69.4) * mm});
            skLineSegment(sketch, "E286.2.2", {"start": v(-87.5, -69.4) * mm, "end": v(-87.5, -66.4) * mm});
            skLineSegment(sketch, "E286.2.3", {"start": v(-87.5, -66.4) * mm, "end": v(-117.5, -66.4) * mm});
            skLineSegment(sketch, "E286.3.0", {"start": v(-17.5, -66.4) * mm, "end": v(-17.5, -69.4) * mm});
            skLineSegment(sketch, "E286.3.1", {"start": v(-17.5, -69.4) * mm, "end": v(-2.5, -69.4) * mm});
            skLineSegment(sketch, "E286.3.2", {"start": v(-2.5, -69.4) * mm, "end": v(12.5, -69.4) * mm});
            skLineSegment(sketch, "E286.3.3", {"start": v(12.5, -69.4) * mm, "end": v(12.5, -66.4) * mm});
            skLineSegment(sketch, "E286.3.4", {"start": v(12.5, -66.4) * mm, "end": v(-17.5, -66.4) * mm});
            skLineSegment(sketch, "E286.4.0", {"start": v(82.5, -69.4) * mm, "end": v(112.5, -69.4) * mm});
            skLineSegment(sketch, "E286.4.1", {"start": v(112.5, -69.4) * mm, "end": v(112.5, -66.4) * mm});
            skLineSegment(sketch, "E286.4.2", {"start": v(112.5, -66.4) * mm, "end": v(82.5, -66.4) * mm});
            skLineSegment(sketch, "E286.4.3", {"start": v(82.5, -66.4) * mm, "end": v(82.5, -69.4) * mm});
            skLineSegment(sketch, "E286.5.0", {"start": v(149.9, -40.5) * mm, "end": v(152.9, -40.5) * mm});
            skLineSegment(sketch, "E286.5.1", {"start": v(152.9, -40.5) * mm, "end": v(152.9, -10.5) * mm});
            skLineSegment(sketch, "E286.5.2", {"start": v(152.9, -10.5) * mm, "end": v(149.9, -10.5) * mm});
            skLineSegment(sketch, "E286.5.3", {"start": v(149.9, -10.5) * mm, "end": v(149.9, -40.5) * mm});
            skLineSegment(sketch, "E286.6.0", {"start": v(152.9, 55.5) * mm, "end": v(152.9, 85.5) * mm});
            skLineSegment(sketch, "E286.6.1", {"start": v(152.9, 85.5) * mm, "end": v(149.9, 85.5) * mm});
            skLineSegment(sketch, "E286.6.2", {"start": v(149.9, 85.5) * mm, "end": v(149.9, 55.5) * mm});
            skLineSegment(sketch, "E286.6.3", {"start": v(149.9, 55.5) * mm, "end": v(152.9, 55.5) * mm});
            skLineSegment(sketch, "E286.7.0", {"start": v(112.5, 114.4) * mm, "end": v(82.5, 114.4) * mm});
            skLineSegment(sketch, "E286.7.1", {"start": v(82.5, 114.4) * mm, "end": v(82.5, 111.4) * mm});
            skLineSegment(sketch, "E286.7.2", {"start": v(82.5, 111.4) * mm, "end": v(112.5, 111.4) * mm});
            skLineSegment(sketch, "E286.7.3", {"start": v(112.5, 111.4) * mm, "end": v(112.5, 114.4) * mm});
            skLineSegment(sketch, "E286.8.0", {"start": v(-2.5, 114.4) * mm, "end": v(-17.5, 114.4) * mm});
            skLineSegment(sketch, "E286.8.1", {"start": v(-17.5, 114.4) * mm, "end": v(-17.5, 111.4) * mm});
            skLineSegment(sketch, "E286.8.2", {"start": v(-17.5, 111.4) * mm, "end": v(12.5, 111.4) * mm});
            skLineSegment(sketch, "E286.8.3", {"start": v(12.5, 111.4) * mm, "end": v(12.5, 114.4) * mm});
            skLineSegment(sketch, "E286.8.4", {"start": v(12.5, 114.4) * mm, "end": v(-2.5, 114.4) * mm});
            skLineSegment(sketch, "E286.9.0", {"start": v(-87.5, 114.4) * mm, "end": v(-117.5, 114.4) * mm});
            skLineSegment(sketch, "E286.9.1", {"start": v(-117.5, 114.4) * mm, "end": v(-117.5, 111.4) * mm});
            skLineSegment(sketch, "E286.9.2", {"start": v(-117.5, 111.4) * mm, "end": v(-87.5, 111.4) * mm});
            skLineSegment(sketch, "E286.9.3", {"start": v(-87.5, 111.4) * mm, "end": v(-87.5, 114.4) * mm});
            skLineSegment(sketch, "E287.0", {"start": v(-157.9, 55.5) * mm, "end": v(-154.9, 55.5) * mm});
            skLineSegment(sketch, "E287.1", {"start": v(-157.9, 85.5) * mm, "end": v(-157.9, 55.5) * mm});
            skLineSegment(sketch, "E287.3", {"start": v(-157.9, 85.5) * mm, "end": v(-154.9, 85.5) * mm});
            skLineSegment(sketch, "E288.0", {"start": v(-154.9, 55.5) * mm, "end": v(-154.9, -10.5) * mm});
            skLineSegment(sketch, "E288.1", {"start": v(-154.9, 85.5) * mm, "end": v(-154.9, 55.5) * mm});
            skLineSegment(sketch, "E289.0", {"start": v(-203.05, 102.56) * mm, "end": v(-203.05, 101.5) * mm});
            skLineSegment(sketch, "E289.1", {"start": v(-200.95, 101.5) * mm, "end": v(-203.05, 101.5) * mm});
            skLineSegment(sketch, "E289.2", {"start": v(-200.95, 102.56) * mm, "end": v(-200.95, 101.5) * mm});
            skCircle(sketch, "E290.0", {"center": v(107.8, 99.8) * mm, "radius": 1.55 * mm});
            skCircle(sketch, "E290.1", {"center": v(-2.5, 106.25) * mm, "radius": 1.55 * mm});
            skCircle(sketch, "E290.2", {"center": v(-112.8, 99.8) * mm, "radius": 1.55 * mm});
            skCircle(sketch, "E290.3", {"center": v(-119.25, 22.5) * mm, "radius": 1.55 * mm});
            skCircle(sketch, "E290.4", {"center": v(-112.8, -54.8) * mm, "radius": 1.55 * mm});
            skCircle(sketch, "E290.5", {"center": v(-2.5, -61.25) * mm, "radius": 1.55 * mm});
            skCircle(sketch, "E290.6", {"center": v(107.8, -54.8) * mm, "radius": 1.55 * mm});
            skCircle(sketch, "E290.7", {"center": v(114.25, 22.5) * mm, "radius": 1.55 * mm});
            skLineSegment(sketch, "E291.0", {"start": v(-234, -67.5) * mm, "end": v(-163.5, -67.5) * mm});
            skLineSegment(sketch, "E291.1", {"start": v(-234, -28) * mm, "end": v(-234, -67.5) * mm});
            skLineSegment(sketch, "E291.2", {"start": v(-234, -28) * mm, "end": v(-163.5, -28) * mm});
            skLineSegment(sketch, "E291.3", {"start": v(-163.5, -28) * mm, "end": v(-163.5, -67.5) * mm});
            skLineSegment(sketch, "E292.0", {"start": v(186, -38) * mm, "end": v(186, -17) * mm});
            skCircle(sketch, "E292.1", {"center": v(192, -17) * mm, "radius": 6 * mm});
            skLineSegment(sketch, "E292.2", {"start": v(198, -38) * mm, "end": v(198, -17) * mm});
            skLineSegment(sketch, "E292.3", {"start": v(198, -38) * mm, "end": v(186, -38) * mm});
            skLineSegment(sketch, "E293.0.0", {"start": v(237, -176.5) * mm, "end": v(237, 155) * mm});
            skLineSegment(sketch, "E293.0.2", {"start": v(229.5, 162.5) * mm, "end": v(-217, 162.5) * mm});
            skLineSegment(sketch, "E293.0.4", {"start": v(-222, 157.5) * mm, "end": v(-222, 145) * mm});
            skArc(sketch, "E293.0.5", {"start": v(-222, 145) * mm, "mid": v(-224.93, 137.93) * mm, "end": v(-232, 135) * mm});
            skLineSegment(sketch, "E293.0.6", {"start": v(-232, 135) * mm, "end": v(-237, 135) * mm});
            skArc(sketch, "E294.0", {"start": v(-192.4, 11.3) * mm, "mid": v(-195.59, 16.17) * mm, "end": v(-200.95, 18.44) * mm});
            skLineSegment(sketch, "E294.1", {"start": v(-191.7, 5.7) * mm, "end": v(-191.7, 11.3) * mm});
            skArc(sketch, "E294.2", {"start": v(-200.95, -1.44) * mm, "mid": v(-195.59, 0.83) * mm, "end": v(-192.4, 5.7) * mm});
            skArc(sketch, "E294.3", {"start": v(-211.6, 5.7) * mm, "mid": v(-208.41, 0.83) * mm, "end": v(-203.05, -1.44) * mm});
            skArc(sketch, "E294.4", {"start": v(-203.05, 18.44) * mm, "mid": v(-208.41, 16.17) * mm, "end": v(-211.6, 11.3) * mm});
            skLineSegment(sketch, "E294.5", {"start": v(-212.3, 5.7) * mm, "end": v(-212.3, 11.3) * mm});
            skLineSegment(sketch, "E294.6", {"start": v(-200.95, -2.5) * mm, "end": v(-203.05, -2.5) * mm});
            skLineSegment(sketch, "E294.7", {"start": v(-200.95, -1.44) * mm, "end": v(-200.95, -2.5) * mm});
            skLineSegment(sketch, "E294.8", {"start": v(-203.05, -1.44) * mm, "end": v(-203.05, -2.5) * mm});
            skLineSegment(sketch, "E294.9", {"start": v(-211.6, 5.7) * mm, "end": v(-212.3, 5.7) * mm});
            skLineSegment(sketch, "E294.10", {"start": v(-211.6, 11.3) * mm, "end": v(-212.3, 11.3) * mm});
            skLineSegment(sketch, "E294.11", {"start": v(-192.4, 11.3) * mm, "end": v(-191.7, 11.3) * mm});
            skLineSegment(sketch, "E294.12", {"start": v(-191.7, 5.7) * mm, "end": v(-192.4, 5.7) * mm});
            skLineSegment(sketch, "E294.13", {"start": v(-200.95, 18.44) * mm, "end": v(-200.95, 19.5) * mm});
            skLineSegment(sketch, "E294.14", {"start": v(-200.95, 19.5) * mm, "end": v(-203.05, 19.5) * mm});
            skLineSegment(sketch, "E294.15", {"start": v(-203.05, 18.44) * mm, "end": v(-203.05, 19.5) * mm});
            skCircle(sketch, "E295.0", {"center": v(169.5, 40) * mm, "radius": 11.8 * mm});
            skCircle(sketch, "E295.1", {"center": v(204.5, 40) * mm, "radius": 11.8 * mm});
            skCircle(sketch, "E295.2", {"center": v(204.5, 71) * mm, "radius": 11.8 * mm});
            skCircle(sketch, "E295.3", {"center": v(169.5, 71) * mm, "radius": 11.8 * mm});
            skCircle(sketch, "E295.4", {"center": v(169.5, 109.5) * mm, "radius": 11.8 * mm});
            skCircle(sketch, "E295.5", {"center": v(212, 102) * mm, "radius": 9.75 * mm});
            skCircle(sketch, "E296.6", {"center": v(157.5, 30.5) * mm, "radius": 1.55 * mm});
            skCircle(sketch, "E296.7", {"center": v(157.5, 61.5) * mm, "radius": 1.55 * mm});
            skCircle(sketch, "E296.8", {"center": v(157.5, 100) * mm, "radius": 1.55 * mm});
            skCircle(sketch, "E296.9", {"center": v(181.5, 80.5) * mm, "radius": 1.55 * mm});
            skCircle(sketch, "E296.10", {"center": v(192.5, 61.5) * mm, "radius": 1.55 * mm});
            skCircle(sketch, "E296.11", {"center": v(216.5, 80.5) * mm, "radius": 1.55 * mm});
            skCircle(sketch, "E296.12", {"center": v(181.5, 49.5) * mm, "radius": 1.55 * mm});
            skCircle(sketch, "E296.13", {"center": v(192.5, 30.5) * mm, "radius": 1.55 * mm});
            skCircle(sketch, "E296.14", {"center": v(216.5, 49.5) * mm, "radius": 1.55 * mm});
            skCircle(sketch, "E296.15", {"center": v(218.25, 91.17) * mm, "radius": 1.75 * mm});
            skCircle(sketch, "E296.16", {"center": v(181.5, 119) * mm, "radius": 1.55 * mm});
            skCircle(sketch, "E296.17", {"center": v(199.5, 102) * mm, "radius": 1.75 * mm});
            skCircle(sketch, "E296.18", {"center": v(218.25, 112.83) * mm, "radius": 1.75 * mm});
            skSolve(sketch);
        }
        {
            var Q0;
            Q0=makeQuery(id+"F9.imprint","IMPRINT",FACE,{"disambiguationData":[TD([[makeQuery(id+"F9.imprint","IMPRINT",EDGE,{"derivedFrom":sQuery(id+"F9.wireOp",EDGE,"E272.13")}),-1.0]])]});
            extrude(context, id + "F10", {"entities" : qUnion([Q0]), "oppositeDirection" : true, "depth" : (getVariable(context, 'PanelThickness')) * mm});
        }
        {
            var Q0;
            Q0=makeQuery(id+"F7.imprint","IMPRINT",FACE,{"disambiguationData":[TD([[makeQuery(id+"F7.imprint","IMPRINT",EDGE,{"derivedFrom":sQuery(id+"F7.wireOp",EDGE,"E227.bottom")}),-1.0]])]});
            extrude(context, id + "F11", {"entities" : qUnion([Q0]), "depth" : (getVariable(context, 'PanelThickness')) * mm});
        }
        {
            var Q0;
            Q0=makeQuery(id+"F9.imprint","IMPRINT",FACE,{"disambiguationData":[TD([[makeQuery(id+"F9.imprint","IMPRINT",EDGE,{"derivedFrom":sQuery(id+"F9.wireOp",EDGE,"E286.0.0")}),1.0]])]});
            extrude(context, id + "F12", {"entities" : qUnion([Q0]), "oppositeDirection" : true, "depth" : (getVariable(context, 'PanelThickness')) * mm});
        }
        {
            var Q0;
            Q0=qCreatedBy(makeId("Top.planeOp"),FACE);
            var sketch = newSketch(context, id + "F13", { "sketchPlane" : qUnion([Q0])});
            skPoint(sketch, "E297.0", {"position": v(-196, -96.5) * mm});
            skPoint(sketch, "E297.1", {"position": v(-196, -166.5) * mm});
            skPoint(sketch, "E297.2", {"position": v(-16, -166.5) * mm});
            skPoint(sketch, "E297.3", {"position": v(-16, -96.5) * mm});
            skLineSegment(sketch, "E298.bottom", {"start": v(-196, -166.5) * mm, "end": v(-16, -166.5) * mm});
            skLineSegment(sketch, "E298.top", {"start": v(-196, -96.5) * mm, "end": v(-16, -96.5) * mm});
            skLineSegment(sketch, "E298.left", {"start": v(-196, -166.5) * mm, "end": v(-196, -96.5) * mm});
            skLineSegment(sketch, "E298.right", {"start": v(-16, -166.5) * mm, "end": v(-16, -96.5) * mm});
            skPoint(sketch, "E299.0", {"position": v(16, -166.5) * mm});
            skPoint(sketch, "E299.1", {"position": v(16, -96.5) * mm});
            skPoint(sketch, "E299.2", {"position": v(196, -96.5) * mm});
            skPoint(sketch, "E299.3", {"position": v(196, -166.5) * mm});
            skLineSegment(sketch, "E300.bottom", {"start": v(16, -166.5) * mm, "end": v(196, -166.5) * mm});
            skLineSegment(sketch, "E300.top", {"start": v(16, -96.5) * mm, "end": v(196, -96.5) * mm});
            skLineSegment(sketch, "E300.left", {"start": v(16, -166.5) * mm, "end": v(16, -96.5) * mm});
            skLineSegment(sketch, "E300.right", {"start": v(196, -166.5) * mm, "end": v(196, -96.5) * mm});
            skPoint(sketch, "E301", {"position": v(-196, -131.5) * mm});
            skPoint(sketch, "E302", {"position": v(-16, -131.5) * mm});
            skPoint(sketch, "E303", {"position": v(16, -131.5) * mm});
            skPoint(sketch, "E304", {"position": v(196, -131.5) * mm});
            skLineSegment(sketch, "E305", {"start": v(-196, -131.5) * mm, "end": v(-16, -131.5) * mm, "construction": true});
            skPoint(sketch, "E306", {"position": v(-151, -131.5) * mm});
            skPoint(sketch, "E307.1.0.0", {"position": v(-106, -131.5) * mm});
            skPoint(sketch, "E307.2.0.0", {"position": v(-61, -131.5) * mm});
            skLineSegment(sketch, "E307.direction1", {"start": v(-151, -131.5) * mm, "end": v(-106, -131.5) * mm, "construction": true});
            skLineSegment(sketch, "E308", {"start": v(-196, -131.5) * mm, "end": v(-151, -131.5) * mm, "construction": true});
            skLineSegment(sketch, "E309", {"start": v(-61, -131.5) * mm, "end": v(-16, -131.5) * mm, "construction": true});
            skCircle(sketch, "E310", {"center": v(-151, -131.5) * mm, "radius": 1.55 * mm});
            skCircle(sketch, "E311", {"center": v(-61, -131.5) * mm, "radius": 1.55 * mm});
            skLineSegment(sketch, "E312", {"start": v(-16, -131.5) * mm, "end": v(16, -131.5) * mm, "construction": true});
            skLineSegment(sketch, "E313", {"start": v(0, -131.5) * mm, "end": v(0, -98.05) * mm, "construction": true});
            skPoint(sketch, "E314", {"position": v(61, -131.5) * mm});
            skPoint(sketch, "E315", {"position": v(106, -131.5) * mm});
            skPoint(sketch, "E316", {"position": v(151, -131.5) * mm});
            skLineSegment(sketch, "E317", {"start": v(16, -131.5) * mm, "end": v(61, -131.5) * mm, "construction": true});
            skLineSegment(sketch, "E318", {"start": v(61, -131.5) * mm, "end": v(106, -131.5) * mm, "construction": true});
            skLineSegment(sketch, "E319", {"start": v(151, -131.5) * mm, "end": v(196, -131.5) * mm, "construction": true});
            skLineSegment(sketch, "E320", {"start": v(106, -131.5) * mm, "end": v(151, -131.5) * mm, "construction": true});
            skCircle(sketch, "E321", {"center": v(61, -131.5) * mm, "radius": 1.55 * mm});
            skCircle(sketch, "E322", {"center": v(151, -131.5) * mm, "radius": 1.55 * mm});
            skSolve(sketch);
        }
        {
            var Q0;
            Q0=qSketchRegion(id+"F13",true);
            extrude(context, id + "F14", {"entities" : qUnion([Q0]), "oppositeDirection" : true, "depth" : (getVariable(context, 'PanelThickness')) * mm});
        }
        {
            var Q0;
            Q0=qCreatedBy(makeId("Top.planeOp"),FACE);
            var sketch = newSketch(context, id + "F15", { "sketchPlane" : qUnion([Q0])});
            skLineSegment(sketch, "E323.0", {"start": v(-242, 130) * mm, "end": v(-242, -184) * mm});
            skArc(sketch, "E323.1", {"start": v(-242, -184) * mm, "mid": v(-239.8, -189.3) * mm, "end": v(-234.5, -191.5) * mm});
            skLineSegment(sketch, "E323.2", {"start": v(-234.5, -191.5) * mm, "end": v(222, -191.5) * mm});
            skArc(sketch, "E323.3", {"start": v(222, -191.5) * mm, "mid": v(232.6, -187.1) * mm, "end": v(237, -176.5) * mm});
            skLineSegment(sketch, "E323.4", {"start": v(237, 155) * mm, "end": v(237, -176.5) * mm});
            skCircle(sketch, "E324.0", {"center": v(151, -131.5) * mm, "radius": 1.55 * mm});
            skCircle(sketch, "E325.0", {"center": v(61, -131.5) * mm, "radius": 1.55 * mm});
            skCircle(sketch, "E326.0", {"center": v(-61, -131.5) * mm, "radius": 1.55 * mm});
            skCircle(sketch, "E327.1", {"center": v(-151, -131.5) * mm, "radius": 1.55 * mm});
            skLineSegment(sketch, "E328.0", {"start": v(-196, -96.5) * mm, "end": v(-16, -96.5) * mm});
            skLineSegment(sketch, "E329", {"start": v(-242, -86.5) * mm, "end": v(237, -86.5) * mm});
            skSolve(sketch);
        }
        {
            var Q0;
            Q0=qSketchRegion(id+"F15",true);
            extrude(context, id + "F16", {"entities" : qUnion([Q0]), "depth" : (getVariable(context, 'PanelThickness')) * mm});
        }
        {
            var Q0;
            Q0=makeQuery(id+"F1.imprint","IMPRINT",FACE,{"disambiguationData":[TD([[makeQuery(id+"F1.imprint","IMPRINT",EDGE,{"derivedFrom":sQuery(id+"F1.wireOp",EDGE,"E4.rect.right")}),-1.0]])]});
            var Q1;
            Q1=makeQuery(id+"F1.imprint","IMPRINT",FACE,{"disambiguationData":[TD([[makeQuery(id+"F1.imprint","IMPRINT",EDGE,{"derivedFrom":sQuery(id+"F1.wireOp",EDGE,"E19.bottom")}),1.0]])]});
            extrude(context, id + "F17", {"entities" : qUnion([Q0, Q1]), "depth" : 3 * mm});
        }
    });
